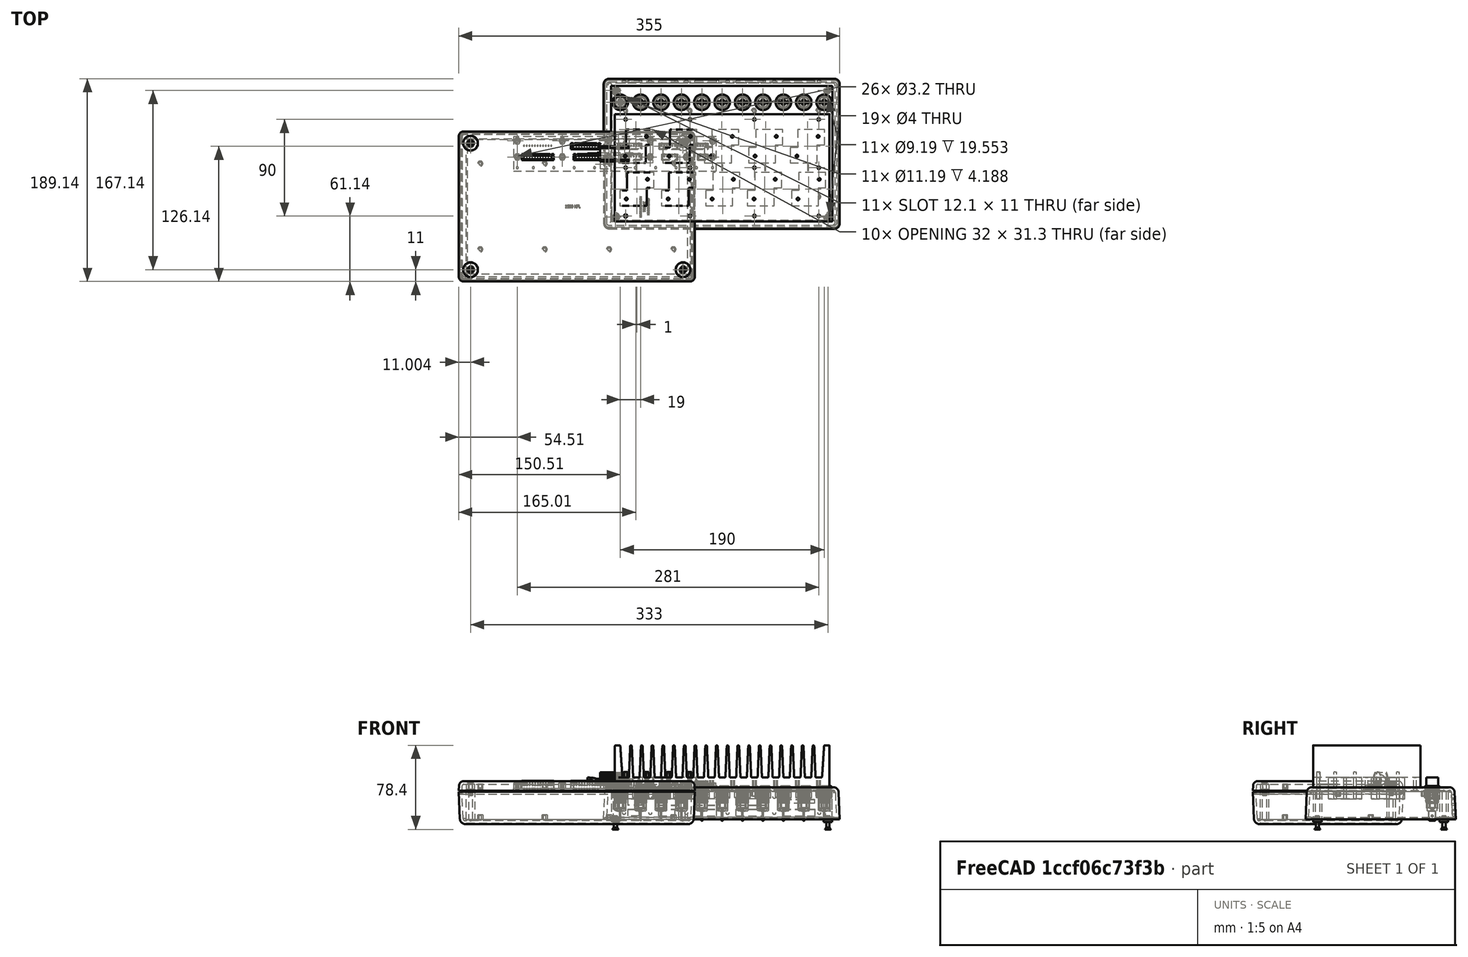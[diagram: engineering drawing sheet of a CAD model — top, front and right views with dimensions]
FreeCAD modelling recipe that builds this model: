
FCSTD DOCUMENT  (FreeCAD 0.20R29410 (Git))
Label: LiPoKiller
License: All rights reserved
LicenseURL: http://en.wikipedia.org/wiki/All_rights_reserved
objects: TechDraw::DrawViewDimension×84, Part::Feature×76, App::Part×52, Part::FeaturePython×17, Sketcher::SketchObject×12, Part::Extrusion×12, Part::MultiFuse×5, TechDraw::DrawSVGTemplate×4, TechDraw::DrawProjGroupItem×4, TechDraw::DrawProjGroup×4, TechDraw::DrawPage×4, Part::Cut×3, App::DocumentObjectGroup×2, Spreadsheet::Sheet×1, PartDesign::CoordinateSystem×1, App::FeaturePython×1, TechDraw::DrawViewBalloon×1
note: 111 computed .brp shape members not serialized (recipe doc carries the construction recipe); baked Part::Feature solids carry a one-line shape summary decoded from their .brp

FEATURE [Spreadsheet::Sheet] Spreadsheet  label="Param"
  cells = A1=R_Grid_Along; B1(R_Grid_Along)=40; A2=R_Grid_Across; B2(R_Grid_Across)=40; A3=R_nof_Along; B3(R_nof_Along)=2; A4=R_nof_Across; B4(R_nof_Across)=5; A5=R_Offset; B5(R_Offset)=1; A6=R_Body_Length; B6(R_Body_Length)=27.3; A7=R_Body_Width; B7(R_Body_Width)=14.2; A8=R_Tab_Length; B8(R_Tab_Length)=10.4; A9=R_Tab_Width; B9(R_Tab_Width)==(28 - 14.2) / 2; A10=R_Clearance; B10(R_Clearance)=2; A11=R_Hole_Along; B11(R_Hole_Along)=18.3; A12=R_Hole_Across; B12(R_Hole_Across)=19.8; A13=R_Hole_Size; B13(R_Hole_Size)=2.5; A14=R_Thread; B14(R_Thread)=M3; A15=Heatsink_Length; B15(Heatsink_Length)=200; A16=Heatsing_Width; B16(Heatsink_Width)=100; A17=Heatsink_Shift; B17(Heatsink_Shift)==26 / 2; A18=Con_Grid; B18(Con_Grid)=19; A19=Con_Pos_y; B19(Con_Pos_y)=48; A20=Con_nof; B20(Con_nof)=11; A21=Con_Diameter; B21(Con_Diameter)=12.1; A22=Con_Width; B22(Con_Width)=11; A23=Heatsink_Hole; B23(Heatsink_Hole)=3.2; A24=Heatsink_Thread_Hole; B24(Heatsink_Thread_Hole)=2.5; A25=Heatsink_Thread; B25(Heatsink_Thread)=M3; A26=Heatsink_Hole_nof_x; B26(Heatsink_Hole_nof_x)=4; A27=Heatsink_Hole_nof_y; B27(Heatsink_Hole_nof_y)=3; A28=Heatsink_Hole_Grid_x; B28(Heatsink_Hole_Grid_x)=60; A29=Heatsink_Hole_Grid_y; B29(Heatsink_Hole_Grid_y)=45; A30=Heatsink_Hole_Offset; B30(Heatsink_Hole_Offset)=5; A31=Balancer_Width; B31(Balancer_Width)=5.75; A32=Balancer_Length_Offset; B32(Balancer_Length_Offset)=2.4; A33=Balancer_Length_Increment; B33(Balancer_Length_Increment)=2.5; A34=Balancer_Clearance; B34(Balancer_Clearance)=0.2; A35=Balancer_Grid; B35(Balancer_Grid)=10; A36=Balancer_Distance; B36(Balancer_Distance)=16.1; A37=Balancer_Pin_Offset; B37(Balancer_Pin_Offset)=3.4; A38=Balancer_Mil_Size; B38(Balancer_Mil_Size)=2.54; A39=Balancer_Mil_Clearance; B39(Balancer_Mil_Clearance)=0.5; A40=Balancer_X; B40(Balancer_X)=72; A41=Balancer_Y; B41(Balancer_Y)=7.5; A42=Panel_Mount_Diameter; B42(Panel_Mount_Diameter)=3.2; A43=Panel_Mount_X; B43(Panel_Mount_X)=91; A44=Panel_Mount_Y; B44(Panel_Mount_Y)=12; A45=Panel_Length; B45(Panel_Length)=189; A46=Panel_Width; B46(Panel_Width)=32
FEATURE [Sketcher::SketchObject] Sketch
  FullyConstrained = true
  expr: Constraints[10] = <<Param>>.R_Tab_Width
  expr: Constraints[11] = <<Param>>.R_Tab_Width
  expr: Constraints[12] = <<Param>>.R_Tab_Length + 2 * <<Param>>.R_Clearance
  expr: Constraints[13] = <<Param>>.R_Tab_Length + 2 * <<Param>>.R_Clearance
  expr: Constraints[20] = <<Param>>.R_Grid_Along * (<<Param>>.R_nof_Along - 1) / 2 + <<Param>>.Heatsink_Shift
  expr: Constraints[29] = <<Param>>.Heatsink_Length / 2 - <<Param>>.R_Grid_Across * (<<Param>>.R_nof_Across - 1) / 2 + <<Param>>.R_Offset / 2
  expr: Constraints[8] = Spreadsheet.R_Body_Width + 2 * <<Param>>.R_Clearance
  expr: Constraints[9] = <<Param>>.R_Body_Length + 2 * <<Param>>.R_Clearance
  sketch-geometry (11):
    g0: LineSegment StartX=4.5 StartY=-48.65 StartZ=0 EndX=29.6 EndY=-48.65 EndZ=0
    g1: LineSegment StartX=29.6 StartY=-48.65 StartZ=0 EndX=29.6 EndY=-31.75 EndZ=0
    g2: LineSegment StartX=29.6 StartY=-31.75 StartZ=0 EndX=36.5 EndY=-31.75 EndZ=0
    g3: LineSegment StartX=36.5 StartY=-31.75 StartZ=0 EndX=36.5 EndY=-17.35 EndZ=0
    g4: LineSegment StartX=36.5 StartY=-17.35 StartZ=0 EndX=11.4 EndY=-17.35 EndZ=0
    g5: LineSegment StartX=11.4 StartY=-17.35 StartZ=0 EndX=11.4 EndY=-34.25 EndZ=0
    g6: LineSegment StartX=11.4 StartY=-34.25 StartZ=0 EndX=4.5 EndY=-34.25 EndZ=0
    g7: LineSegment StartX=4.5 StartY=-34.25 StartZ=0 EndX=4.5 EndY=-48.65 EndZ=0
    g8: LineSegment StartX=11.4 StartY=-17.35 StartZ=0 EndX=29.6 EndY=-48.65 EndZ=0
    g9: LineSegment StartX=11.4 StartY=-34.25 StartZ=0 EndX=29.6 EndY=-31.75 EndZ=0
    g10: GeomPoint X=20.5 Y=-33 Z=0
  constraints (30):
    c: Coincident(g0,g1)
    c: Coincident(g1,g2)
    c: Coincident(g2,g3)
    c: Coincident(g3,g4)
    c: Coincident(g4,g5)
    c: Coincident(g5,g6)
    c: Coincident(g6,g7)
    c: Coincident(g7,g0)
    c: Distance(g5,g1) = 18.2
    c: Distance(g4,g0) = 31.3
    c: Distance(g6,g5) = 6.9
    c: Distance(g1,g2) = 6.9
    c: Distance(g3,g2) = 14.4
    c: Distance(g6,g0) = 14.4
    c: Coincident(g8,g4)
    c: Coincident(g9,g5)
    c: Coincident(g9,g1)
    c: Coincident(g8,g0)
    c: PointOnObject(g10,g9)
    c: PointOnObject(g10,g8)
    c: Distance(g10,g-1) = 33
    c: Perpendicular(g0,g7)
    c: Perpendicular(g0,g1)
    c: Perpendicular(g2,g1)
    c: Perpendicular(g2,g3)
    c: Perpendicular(g3,g4)
    c: Perpendicular(g4,g5)
    c: Perpendicular(g5,g6)
    c: Horizontal(g4)
    c: Distance(g10,g-2) = 20.5
FEATURE [Part::Extrusion] Extrude
  Base = -> Sketch
  Dir = (0,0,1)
  DirMode = 2
  FaceMakerClass = Part::FaceMakerBullseye
  LengthFwd = 10
  LengthRev = 10
  Solid = true
  Symmetric = false
FEATURE [Part::FeaturePython] Array001  # Draft array (typed FeaturePython)
  AlwaysSyncPlacement = false
  Angle = 360
  ArrayType = 0
  Axis = (0,0,1)
  Base = -> Extrude
  Center = (0,0,0)
  Count = 3
  ExpandArray = false
  Fuse = false
  IntervalAxis = (0,0,0)
  IntervalX = (80,0,0)
  IntervalY = (0,80,0)
  IntervalZ = (0,0,0)
  NumberCircles = 3
  NumberPolar = 5
  NumberX = 3
  NumberY = 1
  NumberZ = 1
  PlacementList = 3 placements: arithmetic series from (0,0,0) step (80,0,0) to (160,0,0)
  RadialDistance = 50
  ScaleList = (3) [(1,1,1),(1,1,1),(1,1,1)]
  Symmetry = 1
  TangentialDistance = 25
  expr: .IntervalX.x = <<Param>>.R_Grid_Across * 2
  expr: .IntervalY.y = <<Param>>.R_Grid_Along * 2
  expr: NumberX = ceil(<<Param>>.R_nof_Across / 2)
  expr: NumberY = ceil(<<Param>>.R_nof_Along / 2)
FEATURE [Sketcher::SketchObject] Sketch001
  FullyConstrained = true
  expr: Constraints[10] = <<Param>>.R_Tab_Width
  expr: Constraints[11] = <<Param>>.R_Tab_Width
  expr: Constraints[12] = <<Param>>.R_Tab_Length + 2 * <<Param>>.R_Clearance
  expr: Constraints[13] = <<Param>>.R_Tab_Length + 2 * <<Param>>.R_Clearance
  expr: Constraints[20] = <<Param>>.R_Grid_Along * (<<Param>>.R_nof_Along - 1) / 2 + <<Param>>.Heatsink_Shift
  expr: Constraints[29] = <<Param>>.Heatsink_Length / 2 - <<Param>>.R_Grid_Across * (<<Param>>.R_nof_Across - 3) / 2 - <<Param>>.R_Offset / 2
  expr: Constraints[8] = Spreadsheet.R_Body_Width + 2 * <<Param>>.R_Clearance
  expr: Constraints[9] = <<Param>>.R_Body_Length + 2 * <<Param>>.R_Clearance
  sketch-geometry (11):
    g0: LineSegment StartX=43.5 StartY=-48.65 StartZ=0 EndX=68.6 EndY=-48.65 EndZ=0
    g1: LineSegment StartX=68.6 StartY=-48.65 StartZ=0 EndX=68.6 EndY=-31.75 EndZ=0
    g2: LineSegment StartX=68.6 StartY=-31.75 StartZ=0 EndX=75.5 EndY=-31.75 EndZ=0
    g3: LineSegment StartX=75.5 StartY=-31.75 StartZ=0 EndX=75.5 EndY=-17.35 EndZ=0
    g4: LineSegment StartX=75.5 StartY=-17.35 StartZ=0 EndX=50.4 EndY=-17.35 EndZ=0
    g5: LineSegment StartX=50.4 StartY=-17.35 StartZ=0 EndX=50.4 EndY=-34.25 EndZ=0
    g6: LineSegment StartX=50.4 StartY=-34.25 StartZ=0 EndX=43.5 EndY=-34.25 EndZ=0
    g7: LineSegment StartX=43.5 StartY=-34.25 StartZ=0 EndX=43.5 EndY=-48.65 EndZ=0
    g8: LineSegment StartX=50.4 StartY=-17.35 StartZ=0 EndX=68.6 EndY=-48.65 EndZ=0
    g9: LineSegment StartX=50.4 StartY=-34.25 StartZ=0 EndX=68.6 EndY=-31.75 EndZ=0
    g10: GeomPoint X=59.5 Y=-33 Z=0
  constraints (30):
    c: Coincident(g0,g1)
    c: Coincident(g1,g2)
    c: Coincident(g2,g3)
    c: Coincident(g3,g4)
    c: Coincident(g4,g5)
    c: Coincident(g5,g6)
    c: Coincident(g6,g7)
    c: Coincident(g7,g0)
    c: Distance(g5,g1) = 18.2
    c: Distance(g4,g0) = 31.3
    c: Distance(g6,g5) = 6.9
    c: Distance(g1,g2) = 6.9
    c: Distance(g3,g2) = 14.4
    c: Distance(g6,g0) = 14.4
    c: Coincident(g8,g4)
    c: Coincident(g9,g5)
    c: Coincident(g9,g1)
    c: Coincident(g8,g0)
    c: PointOnObject(g10,g9)
    c: PointOnObject(g10,g8)
    c: Distance(g10,g-1) = 33
    c: Perpendicular(g0,g7)
    c: Perpendicular(g0,g1)
    c: Perpendicular(g2,g1)
    c: Perpendicular(g2,g3)
    c: Perpendicular(g3,g4)
    c: Perpendicular(g4,g5)
    c: Perpendicular(g5,g6)
    c: Horizontal(g4)
    c: Distance(g10,g-2) = 59.5
FEATURE [Part::Extrusion] Extrude001
  Base = -> Sketch001
  Dir = (0,0,1)
  DirMode = 2
  FaceMakerClass = Part::FaceMakerBullseye
  LengthFwd = 10
  LengthRev = 10
  Solid = true
  Symmetric = false
FEATURE [Part::FeaturePython] Array002  # Draft array (typed FeaturePython)
  AlwaysSyncPlacement = false
  Angle = 360
  ArrayType = 0
  Axis = (0,0,1)
  Base = -> Extrude001
  Center = (0,0,0)
  Count = 2
  ExpandArray = false
  Fuse = false
  IntervalAxis = (0,0,0)
  IntervalX = (80,0,0)
  IntervalY = (0,80,0)
  IntervalZ = (0,0,0)
  NumberCircles = 3
  NumberPolar = 5
  NumberX = 2
  NumberY = 1
  NumberZ = 1
  PlacementList = 2 placements: [(0,0,0),(80,0,0)]
  RadialDistance = 50
  ScaleList = (2) [(1,1,1),(1,1,1)]
  Symmetry = 1
  TangentialDistance = 25
  expr: .IntervalX.x = <<Param>>.R_Grid_Across * 2
  expr: .IntervalY.y = <<Param>>.R_Grid_Along * 2
  expr: NumberX = floor(<<Param>>.R_nof_Across / 2)
  expr: NumberY = floor(<<Param>>.R_nof_Along / 2)
FEATURE [Sketcher::SketchObject] Sketch002
  FullyConstrained = true
  expr: Constraints[10] = <<Param>>.R_Tab_Width
  expr: Constraints[11] = <<Param>>.R_Tab_Width
  expr: Constraints[12] = <<Param>>.R_Tab_Length + 2 * <<Param>>.R_Clearance
  expr: Constraints[13] = <<Param>>.R_Tab_Length + 2 * <<Param>>.R_Clearance
  expr: Constraints[28] = <<Param>>.Heatsink_Length / 2 - <<Param>>.R_Grid_Across * (<<Param>>.R_nof_Across - 1) / 2 - <<Param>>.R_Offset / 2
  expr: Constraints[31] = <<Param>>.R_Grid_Along * (<<Param>>.R_nof_Along - 1) / 2 + <<Param>>.Heatsink_Shift
  expr: Constraints[33] = <<Param>>.R_Grid_Along
  expr: Constraints[8] = Spreadsheet.R_Body_Width + 2 * <<Param>>.R_Clearance
  expr: Constraints[9] = <<Param>>.R_Body_Length + 2 * <<Param>>.R_Clearance
  sketch-geometry (12):
    g0: LineSegment StartX=3.5 StartY=-8.65 StartZ=0 EndX=28.6 EndY=-8.65 EndZ=0
    g1: LineSegment StartX=28.6 StartY=-8.65 StartZ=0 EndX=28.6 EndY=8.25 EndZ=0
    g2: LineSegment StartX=28.6 StartY=8.25 StartZ=0 EndX=35.5 EndY=8.25 EndZ=0
    g3: LineSegment StartX=35.5 StartY=8.25 StartZ=0 EndX=35.5 EndY=22.65 EndZ=0
    g4: LineSegment StartX=35.5 StartY=22.65 StartZ=0 EndX=10.4 EndY=22.65 EndZ=0
    g5: LineSegment StartX=10.4 StartY=22.65 StartZ=0 EndX=10.4 EndY=5.75 EndZ=0
    g6: LineSegment StartX=10.4 StartY=5.75 StartZ=0 EndX=3.5 EndY=5.75 EndZ=0
    g7: LineSegment StartX=3.5 StartY=5.75 StartZ=0 EndX=3.5 EndY=-8.65 EndZ=0
    g8: LineSegment StartX=10.4 StartY=22.65 StartZ=0 EndX=28.6 EndY=-8.65 EndZ=0
    g9: LineSegment StartX=10.4 StartY=5.75 StartZ=0 EndX=28.6 EndY=8.25 EndZ=0
    g10: GeomPoint X=19.5 Y=7 Z=0
    g11: LineSegment StartX=0 StartY=-33 StartZ=0 EndX=200 EndY=-33 EndZ=0
  constraints (34):
    c: Coincident(g0,g1)
    c: Coincident(g1,g2)
    c: Coincident(g2,g3)
    c: Coincident(g3,g4)
    c: Coincident(g4,g5)
    c: Coincident(g5,g6)
    c: Coincident(g6,g7)
    c: Coincident(g7,g0)
    c: Distance(g5,g1) = 18.2
    c: Distance(g4,g0) = 31.3
    c: Distance(g6,g5) = 6.9
    c: Distance(g1,g2) = 6.9
    c: Distance(g3,g2) = 14.4
    c: Distance(g6,g0) = 14.4
    c: Coincident(g8,g4)
    c: Coincident(g9,g5)
    c: Coincident(g9,g1)
    c: Coincident(g8,g0)
    c: PointOnObject(g10,g9)
    c: PointOnObject(g10,g8)
    c: Perpendicular(g0,g7)
    c: Perpendicular(g0,g1)
    c: Perpendicular(g2,g1)
    c: Perpendicular(g2,g3)
    c: Perpendicular(g3,g4)
    c: Perpendicular(g4,g5)
    c: Perpendicular(g5,g6)
    c: Horizontal(g4)
    c: Distance(g10,g-2) = 19.5
    c: PointOnObject(g11,g-2)
    c: Horizontal(g11)
    c: Distance(g11,g-1) = 33
    c: Distance(g11,g-2) = 200
    c: Distance(g10,g11) = 40
FEATURE [Part::Extrusion] Extrude002
  Base = -> Sketch002
  Dir = (0,0,1)
  DirMode = 2
  FaceMakerClass = Part::FaceMakerBullseye
  LengthFwd = 10
  LengthRev = 10
  Solid = true
  Symmetric = false
FEATURE [Part::FeaturePython] Array003  # Draft array (typed FeaturePython)
  AlwaysSyncPlacement = false
  Angle = 360
  ArrayType = 0
  Axis = (0,0,1)
  Base = -> Extrude002
  Center = (0,0,0)
  Count = 3
  ExpandArray = false
  Fuse = false
  IntervalAxis = (0,0,0)
  IntervalX = (80,0,0)
  IntervalY = (0,80,0)
  IntervalZ = (0,0,0)
  NumberCircles = 3
  NumberPolar = 5
  NumberX = 3
  NumberY = 1
  NumberZ = 1
  PlacementList = 3 placements: arithmetic series from (0,0,0) step (80,0,0) to (160,0,0)
  RadialDistance = 50
  ScaleList = (3) [(1,1,1),(1,1,1),(1,1,1)]
  Symmetry = 1
  TangentialDistance = 25
  expr: .IntervalX.x = <<Param>>.R_Grid_Across * 2
  expr: .IntervalY.y = <<Param>>.R_Grid_Along * 2
  expr: NumberX = ceil(<<Param>>.R_nof_Across / 2)
  expr: NumberY = floor(<<Param>>.R_nof_Along / 2)
FEATURE [Sketcher::SketchObject] Sketch003
  FullyConstrained = true
  expr: Constraints[10] = <<Param>>.R_Tab_Width
  expr: Constraints[11] = <<Param>>.R_Tab_Width
  expr: Constraints[12] = <<Param>>.R_Tab_Length + 2 * <<Param>>.R_Clearance
  expr: Constraints[13] = <<Param>>.R_Tab_Length + 2 * <<Param>>.R_Clearance
  expr: Constraints[28] = <<Param>>.Heatsink_Length / 2 - <<Param>>.R_Grid_Across * (<<Param>>.R_nof_Across - 3) / 2 + <<Param>>.R_Offset / 2
  expr: Constraints[31] = <<Param>>.R_Grid_Along * (<<Param>>.R_nof_Along - 1) / 2 + <<Param>>.Heatsink_Shift
  expr: Constraints[33] = <<Param>>.R_Grid_Along
  expr: Constraints[8] = Spreadsheet.R_Body_Width + 2 * <<Param>>.R_Clearance
  expr: Constraints[9] = <<Param>>.R_Body_Length + 2 * <<Param>>.R_Clearance
  sketch-geometry (12):
    g0: LineSegment StartX=44.5 StartY=-8.65 StartZ=0 EndX=69.6 EndY=-8.65 EndZ=0
    g1: LineSegment StartX=69.6 StartY=-8.65 StartZ=0 EndX=69.6 EndY=8.25 EndZ=0
    g2: LineSegment StartX=69.6 StartY=8.25 StartZ=0 EndX=76.5 EndY=8.25 EndZ=0
    g3: LineSegment StartX=76.5 StartY=8.25 StartZ=0 EndX=76.5 EndY=22.65 EndZ=0
    g4: LineSegment StartX=76.5 StartY=22.65 StartZ=0 EndX=51.4 EndY=22.65 EndZ=0
    g5: LineSegment StartX=51.4 StartY=22.65 StartZ=0 EndX=51.4 EndY=5.75 EndZ=0
    g6: LineSegment StartX=51.4 StartY=5.75 StartZ=0 EndX=44.5 EndY=5.75 EndZ=0
    g7: LineSegment StartX=44.5 StartY=5.75 StartZ=0 EndX=44.5 EndY=-8.65 EndZ=0
    g8: LineSegment StartX=51.4 StartY=22.65 StartZ=0 EndX=69.6 EndY=-8.65 EndZ=0
    g9: LineSegment StartX=51.4 StartY=5.75 StartZ=0 EndX=69.6 EndY=8.25 EndZ=0
    g10: GeomPoint X=60.5 Y=7 Z=0
    g11: LineSegment StartX=0 StartY=-33 StartZ=0 EndX=200 EndY=-33 EndZ=0
  constraints (34):
    c: Coincident(g0,g1)
    c: Coincident(g1,g2)
    c: Coincident(g2,g3)
    c: Coincident(g3,g4)
    c: Coincident(g4,g5)
    c: Coincident(g5,g6)
    c: Coincident(g6,g7)
    c: Coincident(g7,g0)
    c: Distance(g5,g1) = 18.2
    c: Distance(g4,g0) = 31.3
    c: Distance(g6,g5) = 6.9
    c: Distance(g1,g2) = 6.9
    c: Distance(g3,g2) = 14.4
    c: Distance(g6,g0) = 14.4
    c: Coincident(g8,g4)
    c: Coincident(g9,g5)
    c: Coincident(g9,g1)
    c: Coincident(g8,g0)
    c: PointOnObject(g10,g9)
    c: PointOnObject(g10,g8)
    c: Perpendicular(g0,g7)
    c: Perpendicular(g0,g1)
    c: Perpendicular(g2,g1)
    c: Perpendicular(g2,g3)
    c: Perpendicular(g3,g4)
    c: Perpendicular(g4,g5)
    c: Perpendicular(g5,g6)
    c: Horizontal(g4)
    c: Distance(g10,g-2) = 60.5
    c: PointOnObject(g11,g-2)
    c: Horizontal(g11)
    c: Distance(g11,g-1) = 33
    c: Distance(g11,g-2) = 200
    c: Distance(g10,g11) = 40
FEATURE [Part::Extrusion] Extrude003
  Base = -> Sketch003
  Dir = (0,0,1)
  DirMode = 2
  FaceMakerClass = Part::FaceMakerBullseye
  LengthFwd = 10
  LengthRev = 10
  Solid = true
  Symmetric = false
FEATURE [Part::FeaturePython] Array004  # Draft array (typed FeaturePython)
  AlwaysSyncPlacement = false
  Angle = 360
  ArrayType = 0
  Axis = (0,0,1)
  Base = -> Extrude003
  Center = (0,0,0)
  Count = 2
  ExpandArray = false
  Fuse = false
  IntervalAxis = (0,0,0)
  IntervalX = (80,0,0)
  IntervalY = (0,80,0)
  IntervalZ = (0,0,0)
  NumberCircles = 3
  NumberPolar = 5
  NumberX = 2
  NumberY = 1
  NumberZ = 1
  PlacementList = 2 placements: [(0,0,0),(80,0,0)]
  RadialDistance = 50
  ScaleList = (2) [(1,1,1),(1,1,1)]
  Symmetry = 1
  TangentialDistance = 25
  expr: .IntervalX.x = <<Param>>.R_Grid_Across * 2
  expr: .IntervalY.y = <<Param>>.R_Grid_Along * 2
  expr: NumberX = floor(<<Param>>.R_nof_Across / 2)
  expr: NumberY = floor(<<Param>>.R_nof_Along / 2)
FEATURE [Part::Feature] Part__Feature012  label="Resistor Arcol HS"
  shape: bbox 27.3 x 28 x 14.8 mm, 83 faces (baked)
FEATURE [Part::Feature] Part__Feature013  label="Resistor Arcol HS001"
  shape: bbox 33.3 x 2.1 x 2.1 mm, 3 faces (baked)
FEATURE [Part::Feature] Part__Feature014  label="Resistor Arcol HS002"
  shape: bbox 8.85 x 0.8 x 4.5 mm, 7 faces (baked)
FEATURE [Part::Feature] Part__Feature015  label="Resistor Arcol HS003"
  shape: bbox 8.85 x 0.8 x 4.5 mm, 7 faces (baked)
FEATURE [Part::Feature] Part__Feature016  label="Resistor Arcol HS004"
  shape: bbox 27.3 x 9.23 x 9.23 mm, 6 faces, 0 solids (baked)
FEATURE [App::Part] Resistor_Arcol_HS  label="Resistor Arcol HS005"
  Group = -> [Part__Feature012,Part__Feature013,Part__Feature014,Part__Feature015,Part__Feature016]
  Origin = -> Origin002
  Placement = pos=(20.5,-33,2.8e-15) rot=(0.707107,0.707107,0;3.14159rad)
  expr: .Placement.Base.x = <<Param>>.Heatsink_Length / 2 - <<Param>>.R_Grid_Across * (<<Param>>.R_nof_Across - 1) / 2 + <<Param>>.R_Offset / 2
  expr: .Placement.Base.y = -(<<Param>>.R_Grid_Along * (<<Param>>.R_nof_Along - 1) / 2 + <<Param>>.Heatsink_Shift)
FEATURE [Part::FeaturePython] Array005  # Draft array (typed FeaturePython)
  AlwaysSyncPlacement = false
  Angle = 360
  ArrayType = 0
  Axis = (0,0,1)
  Base = -> Resistor_Arcol_HS
  Center = (0,0,0)
  Count = 3
  ExpandArray = false
  Fuse = false
  IntervalAxis = (0,0,0)
  IntervalX = (80,0,0)
  IntervalY = (0,80,0)
  IntervalZ = (0,0,0)
  NumberCircles = 3
  NumberPolar = 5
  NumberX = 3
  NumberY = 1
  NumberZ = 1
  PlacementList = 3 placements: arithmetic series from (20.5,-33,2.8e-15) step (80,0,0) to (180.5,-33,2.8e-15)
  RadialDistance = 50
  ScaleList = (3) [(1,1,1),(1,1,1),(1,1,1)]
  Symmetry = 1
  TangentialDistance = 25
  expr: .IntervalX.x = <<Param>>.R_Grid_Across * 2
  expr: .IntervalY.y = <<Param>>.R_Grid_Along * 2
  expr: NumberX = ceil(<<Param>>.R_nof_Across / 2)
  expr: NumberY = ceil(<<Param>>.R_nof_Along / 2)
FEATURE [Part::Feature] Part__Feature017  label="Resistor Arcol HS006"
  shape: bbox 27.3 x 28 x 14.8 mm, 83 faces (baked)
FEATURE [Part::Feature] Part__Feature018  label="Resistor Arcol HS007"
  shape: bbox 33.3 x 2.1 x 2.1 mm, 3 faces (baked)
FEATURE [Part::Feature] Part__Feature019  label="Resistor Arcol HS008"
  shape: bbox 8.85 x 0.8 x 4.5 mm, 7 faces (baked)
FEATURE [Part::Feature] Part__Feature020  label="Resistor Arcol HS009"
  shape: bbox 8.85 x 0.8 x 4.5 mm, 7 faces (baked)
FEATURE [Part::Feature] Part__Feature021  label="Resistor Arcol HS010"
  shape: bbox 27.3 x 9.23 x 9.23 mm, 6 faces, 0 solids (baked)
FEATURE [App::Part] Resistor_Arcol_HS001  label="Resistor Arcol HS011"
  Group = -> [Part__Feature017,Part__Feature018,Part__Feature019,Part__Feature020,Part__Feature021]
  Origin = -> Origin003
  Placement = pos=(59.5,-33,2.8e-15) rot=(0.707107,0.707107,0;3.14159rad)
  expr: .Placement.Base.x = <<Param>>.Heatsink_Length / 2 - <<Param>>.R_Grid_Across * (<<Param>>.R_nof_Across - 3) / 2 - <<Param>>.R_Offset / 2
  expr: .Placement.Base.y = -(<<Param>>.R_Grid_Along * (<<Param>>.R_nof_Along - 1) / 2 + <<Param>>.Heatsink_Shift)
FEATURE [Part::FeaturePython] Array006  # Draft array (typed FeaturePython)
  AlwaysSyncPlacement = false
  Angle = 360
  ArrayType = 0
  Axis = (0,0,1)
  Base = -> Resistor_Arcol_HS001
  Center = (0,0,0)
  Count = 2
  ExpandArray = false
  Fuse = false
  IntervalAxis = (0,0,0)
  IntervalX = (80,0,0)
  IntervalY = (0,80,0)
  IntervalZ = (0,0,0)
  NumberCircles = 3
  NumberPolar = 5
  NumberX = 2
  NumberY = 1
  NumberZ = 1
  PlacementList = 2 placements: [(59.5,-33,2.8e-15),(139.5,-33,2.8e-15)]
  RadialDistance = 50
  ScaleList = (2) [(1,1,1),(1,1,1)]
  Symmetry = 1
  TangentialDistance = 25
  expr: .IntervalX.x = <<Param>>.R_Grid_Across * 2
  expr: .IntervalY.y = <<Param>>.R_Grid_Along * 2
  expr: NumberX = floor(<<Param>>.R_nof_Across / 2)
  expr: NumberY = floor(<<Param>>.R_nof_Along / 2)
FEATURE [Part::Feature] Part__Feature022  label="Resistor Arcol HS012"
  shape: bbox 27.3 x 28 x 14.8 mm, 83 faces (baked)
FEATURE [Part::Feature] Part__Feature023  label="Resistor Arcol HS013"
  shape: bbox 33.3 x 2.1 x 2.1 mm, 3 faces (baked)
FEATURE [Part::Feature] Part__Feature024  label="Resistor Arcol HS014"
  shape: bbox 8.85 x 0.8 x 4.5 mm, 7 faces (baked)
FEATURE [Part::Feature] Part__Feature025  label="Resistor Arcol HS015"
  shape: bbox 8.85 x 0.8 x 4.5 mm, 7 faces (baked)
FEATURE [Part::Feature] Part__Feature026  label="Resistor Arcol HS016"
  shape: bbox 27.3 x 9.23 x 9.23 mm, 6 faces, 0 solids (baked)
FEATURE [App::Part] Resistor_Arcol_HS002  label="Resistor Arcol HS017"
  Group = -> [Part__Feature022,Part__Feature023,Part__Feature024,Part__Feature025,Part__Feature026]
  Origin = -> Origin004
  Placement = pos=(19.5,7,2.8e-15) rot=(0.707107,0.707107,0;3.14159rad)
  expr: .Placement.Base.x = <<Param>>.Heatsink_Length / 2 - <<Param>>.R_Grid_Across * (<<Param>>.R_nof_Across - 1) / 2 - <<Param>>.R_Offset / 2
  expr: .Placement.Base.y = -(<<Param>>.R_Grid_Along * (<<Param>>.R_nof_Along - 1) / 2 + <<Param>>.Heatsink_Shift) + <<Param>>.R_Grid_Along
FEATURE [Part::FeaturePython] Array007  # Draft array (typed FeaturePython)
  AlwaysSyncPlacement = false
  Angle = 360
  ArrayType = 0
  Axis = (0,0,1)
  Base = -> Resistor_Arcol_HS002
  Center = (0,0,0)
  Count = 3
  ExpandArray = false
  Fuse = false
  IntervalAxis = (0,0,0)
  IntervalX = (80,0,0)
  IntervalY = (0,80,0)
  IntervalZ = (0,0,0)
  NumberCircles = 3
  NumberPolar = 5
  NumberX = 3
  NumberY = 1
  NumberZ = 1
  PlacementList = 3 placements: arithmetic series from (19.5,7,2.8e-15) step (80,0,0) to (179.5,7,2.8e-15)
  RadialDistance = 50
  ScaleList = (3) [(1,1,1),(1,1,1),(1,1,1)]
  Symmetry = 1
  TangentialDistance = 25
  expr: .IntervalX.x = <<Param>>.R_Grid_Across * 2
  expr: .IntervalY.y = <<Param>>.R_Grid_Along * 2
  expr: NumberX = ceil(<<Param>>.R_nof_Across / 2)
  expr: NumberY = floor(<<Param>>.R_nof_Along / 2)
FEATURE [Part::Feature] Part__Feature027  label="Resistor Arcol HS018"
  shape: bbox 27.3 x 28 x 14.8 mm, 83 faces (baked)
FEATURE [Part::Feature] Part__Feature028  label="Resistor Arcol HS019"
  shape: bbox 33.3 x 2.1 x 2.1 mm, 3 faces (baked)
FEATURE [Part::Feature] Part__Feature029  label="Resistor Arcol HS020"
  shape: bbox 8.85 x 0.8 x 4.5 mm, 7 faces (baked)
FEATURE [Part::Feature] Part__Feature030  label="Resistor Arcol HS021"
  shape: bbox 8.85 x 0.8 x 4.5 mm, 7 faces (baked)
FEATURE [Part::Feature] Part__Feature031  label="Resistor Arcol HS022"
  shape: bbox 27.3 x 9.23 x 9.23 mm, 6 faces, 0 solids (baked)
FEATURE [App::Part] Resistor_Arcol_HS003  label="Resistor Arcol HS023"
  Group = -> [Part__Feature027,Part__Feature028,Part__Feature029,Part__Feature030,Part__Feature031]
  Origin = -> Origin005
  Placement = pos=(60.5,7,2.8e-15) rot=(0.707107,0.707107,0;3.14159rad)
  expr: .Placement.Base.x = <<Param>>.Heatsink_Length / 2 - <<Param>>.R_Grid_Across * (<<Param>>.R_nof_Across - 3) / 2 + <<Param>>.R_Offset / 2
  expr: .Placement.Base.y = -(<<Param>>.R_Grid_Along * (<<Param>>.R_nof_Along - 1) / 2 + <<Param>>.Heatsink_Shift) + <<Param>>.R_Grid_Along
FEATURE [Part::FeaturePython] Array008  # Draft array (typed FeaturePython)
  AlwaysSyncPlacement = false
  Angle = 360
  ArrayType = 0
  Axis = (0,0,1)
  Base = -> Resistor_Arcol_HS003
  Center = (0,0,0)
  Count = 2
  ExpandArray = false
  Fuse = false
  IntervalAxis = (0,0,0)
  IntervalX = (80,0,0)
  IntervalY = (0,80,0)
  IntervalZ = (0,0,0)
  NumberCircles = 3
  NumberPolar = 5
  NumberX = 2
  NumberY = 1
  NumberZ = 1
  PlacementList = 2 placements: [(60.5,7,2.8e-15),(140.5,7,2.8e-15)]
  RadialDistance = 50
  ScaleList = (2) [(1,1,1),(1,1,1)]
  Symmetry = 1
  TangentialDistance = 25
  expr: .IntervalX.x = <<Param>>.R_Grid_Across * 2
  expr: .IntervalY.y = <<Param>>.R_Grid_Along * 2
  expr: NumberX = floor(<<Param>>.R_nof_Across / 2)
  expr: NumberY = floor(<<Param>>.R_nof_Along / 2)
FEATURE [Part::MultiFuse] Fusion
  Shapes = -> [Array001,Array002,Array003,Array004]
FEATURE [Sketcher::SketchObject] Sketch004
  FullyConstrained = true
  expr: Constraints[10] = <<Param>>.Con_Pos_y
  expr: Constraints[12] = <<Param>>.Heatsink_Length / 2 - <<Param>>.Con_Grid * (<<Param>>.Con_nof - 1) / 2
  expr: Constraints[6] = <<Param>>.Con_Diameter
  expr: Constraints[7] = <<Param>>.Con_Diameter
  expr: Constraints[8] = <<Param>>.Con_Width
  expr: Constraints[9] = <<Param>>.Con_Width / 2
  sketch-geometry (4):
    g0: ArcOfCircle CenterX=5 CenterY=48 CenterZ=0 NormalX=0 NormalY=0 NormalZ=1 AngleXU=0 Radius=6.05 StartAngle=2.0005 EndAngle=4.28269
    g1: ArcOfCircle CenterX=5 CenterY=48 CenterZ=0 NormalX=0 NormalY=0 NormalZ=1 AngleXU=0 Radius=6.05 StartAngle=5.14209 EndAngle=7.42428
    g2: LineSegment StartX=2.47958 StartY=53.5 StartZ=0 EndX=7.52042 EndY=53.5 EndZ=0
    g3: LineSegment StartX=7.52042 StartY=42.5 StartZ=0 EndX=2.47958 EndY=42.5 EndZ=0
  constraints (13):
    c: Coincident(g1,g0)
    c: Coincident(g2,g0)
    c: Coincident(g2,g1)
    c: Coincident(g3,g1)
    c: Coincident(g3,g0)
    c: Horizontal(g3)
    c: Diameter(g1) = 12.1
    c: Diameter(g0) = 12.1
    c: Distance(g1,g3) = 11
    c: Distance(g0,g3) = 5.5
    c: Distance(g0,g-1) = 48
    c: Horizontal(g2)
    c: Distance(g0,g-2) = 5
FEATURE [Part::Extrusion] Extrude004
  Base = -> Sketch004
  Dir = (0,0,1)
  DirMode = 2
  FaceMakerClass = Part::FaceMakerBullseye
  LengthFwd = 10
  LengthRev = 10
  Solid = true
  Symmetric = false
FEATURE [Part::FeaturePython] Array009  # Draft array (typed FeaturePython)
  AlwaysSyncPlacement = false
  Angle = 360
  ArrayType = 0
  Axis = (0,0,1)
  Base = -> Extrude004
  Center = (0,0,0)
  Count = 11
  ExpandArray = false
  Fuse = false
  IntervalAxis = (0,0,0)
  IntervalX = (19,0,0)
  IntervalY = (0,100,0)
  IntervalZ = (0,0,100)
  NumberCircles = 3
  NumberPolar = 5
  NumberX = 11
  NumberY = 1
  NumberZ = 1
  PlacementList = 11 placements: arithmetic series from (0,0,0) step (19,0,0) to (190,0,0)
  RadialDistance = 50
  ScaleList = (11) [(1,1,1),(1,1,1),(1,1,1),(1,1,1),(1,1,1),(1,1,1),(1,1,1),(1,1,1),(1,1,1),(1,1,1),(1,1,1)]
  Symmetry = 1
  TangentialDistance = 25
FEATURE [Part::MultiFuse] Fusion001
  Shapes = -> [Array009,Fusion]
FEATURE [Sketcher::SketchObject] Sketch005
  FullyConstrained = true
  expr: Constraints[1] = <<Param>>.R_Grid_Along * (<<Param>>.R_nof_Along - 1) / 2 + <<Param>>.Heatsink_Shift
  expr: Constraints[26] = <<Param>>.R_Hole_Size
  expr: Constraints[27] = <<Param>>.R_Hole_Size
  expr: Constraints[28] = <<Param>>.R_Hole_Size
  expr: Constraints[29] = <<Param>>.R_Hole_Size
  expr: Constraints[2] = <<Param>>.Heatsink_Length / 2 - <<Param>>.R_Grid_Across * (<<Param>>.R_nof_Across - 1) / 2 + <<Param>>.R_Offset / 2
  expr: Constraints[30] = <<Param>>.R_Hole_Size
  expr: Constraints[31] = <<Param>>.R_Hole_Size
  expr: Constraints[32] = <<Param>>.R_Hole_Size
  expr: Constraints[33] = <<Param>>.R_Hole_Size
  expr: Constraints[8] = <<Param>>.R_Hole_Across
  expr: Constraints[9] = <<Param>>.R_Hole_Along
  sketch-geometry (12):
    g0: LineSegment StartX=30.4 StartY=-23.85 StartZ=0 EndX=10.6 EndY=-42.15 EndZ=0
    g1: GeomPoint X=20.5 Y=-33 Z=0
    g2: LineSegment StartX=20.5 StartY=-33 StartZ=0 EndX=30.4 EndY=-23.85 EndZ=0
    g3: LineSegment StartX=20.5 StartY=-33 StartZ=0 EndX=10.6 EndY=-42.15 EndZ=0
    g4: ArcOfCircle CenterX=30.4 CenterY=-23.85 CenterZ=0 NormalX=0 NormalY=0 NormalZ=1 AngleXU=0 Radius=1.25 StartAngle=1e-16 EndAngle=1.5708
    g5: ArcOfCircle CenterX=30.4 CenterY=-23.85 CenterZ=0 NormalX=0 NormalY=0 NormalZ=1 AngleXU=0 Radius=1.25 StartAngle=1.5708 EndAngle=3.14159
    g6: ArcOfCircle CenterX=30.4 CenterY=-23.85 CenterZ=0 NormalX=0 NormalY=0 NormalZ=1 AngleXU=0 Radius=1.25 StartAngle=3.14159 EndAngle=4.71239
    g7: ArcOfCircle CenterX=30.4 CenterY=-23.85 CenterZ=0 NormalX=0 NormalY=0 NormalZ=1 AngleXU=0 Radius=1.25 StartAngle=4.71239 EndAngle=6.28319
    g8: ArcOfCircle CenterX=10.6 CenterY=-42.15 CenterZ=0 NormalX=0 NormalY=0 NormalZ=1 AngleXU=0 Radius=1.25 StartAngle=0 EndAngle=1.5708
    g9: ArcOfCircle CenterX=10.6 CenterY=-42.15 CenterZ=0 NormalX=0 NormalY=0 NormalZ=1 AngleXU=0 Radius=1.25 StartAngle=1.5708 EndAngle=3.14159
    g10: ArcOfCircle CenterX=10.6 CenterY=-42.15 CenterZ=0 NormalX=0 NormalY=0 NormalZ=1 AngleXU=0 Radius=1.25 StartAngle=3.14159 EndAngle=4.71239
    g11: ArcOfCircle CenterX=10.6 CenterY=-42.15 CenterZ=0 NormalX=0 NormalY=0 NormalZ=1 AngleXU=0 Radius=1.25 StartAngle=4.71239 EndAngle=6.28319
  constraints (42):
    c: PointOnObject(g1,g0)
    c: Distance(g1,g-1) = 33
    c: Distance(g1,g-2) = 20.5
    c: Coincident(g2,g1)
    c: Coincident(g3,g1)
    c: Equal(g2,g3)
    c: Coincident(g0,g3)
    c: Coincident(g0,g2)
    c: DistanceX(g0,g0) = 19.8
    c: DistanceY(g0,g0) = 18.3
    c: Horizontal(g9,g9)
    c: Horizontal(g8,g8)
    c: Horizontal(g11,g11)
    c: Horizontal(g10,g10)
    c: Horizontal(g4,g4)
    c: Horizontal(g7,g7)
    c: Horizontal(g6,g6)
    c: Horizontal(g5,g5)
    c: Vertical(g5,g5)
    c: Vertical(g4,g4)
    c: Vertical(g7,g7)
    c: Vertical(g6,g6)
    c: Vertical(g8,g8)
    c: Vertical(g9,g9)
    c: Vertical(g10,g10)
    c: Vertical(g11,g11)
    c: Diameter(g11) = 2.5
    c: Diameter(g8) = 2.5
    c: Diameter(g9) = 2.5
    c: Diameter(g10) = 2.5
    c: Diameter(g4) = 2.5
    c: Diameter(g5) = 2.5
    c: Diameter(g6) = 2.5
    c: Diameter(g7) = 2.5
    c: Coincident(g5,g0)
    c: Coincident(g4,g5)
    c: Coincident(g6,g4)
    c: Coincident(g7,g4)
    c: Coincident(g8,g0)
    c: Coincident(g9,g8)
    c: Coincident(g10,g8)
    c: Coincident(g11,g8)
FEATURE [Part::Extrusion] Extrude005
  Base = -> Sketch005
  Dir = (0,0,1)
  DirMode = 2
  FaceMakerClass = Part::FaceMakerBullseye
  LengthFwd = 15
  LengthRev = 10
  Solid = true
  Symmetric = false
FEATURE [Part::FeaturePython] Array010  # Draft array (typed FeaturePython)
  AlwaysSyncPlacement = false
  Angle = 360
  ArrayType = 0
  Axis = (0,0,1)
  Base = -> Extrude005
  Center = (0,0,0)
  Count = 3
  ExpandArray = false
  Fuse = false
  IntervalAxis = (0,0,0)
  IntervalX = (80,0,0)
  IntervalY = (0,80,0)
  IntervalZ = (0,0,0)
  NumberCircles = 3
  NumberPolar = 5
  NumberX = 3
  NumberY = 1
  NumberZ = 1
  PlacementList = 3 placements: arithmetic series from (0,0,0) step (80,0,0) to (160,0,0)
  RadialDistance = 50
  ScaleList = (3) [(1,1,1),(1,1,1),(1,1,1)]
  Symmetry = 1
  TangentialDistance = 25
  expr: .IntervalX.x = <<Param>>.R_Grid_Across * 2
  expr: .IntervalY.y = <<Param>>.R_Grid_Along * 2
  expr: NumberX = ceil(<<Param>>.R_nof_Across / 2)
  expr: NumberY = ceil(<<Param>>.R_nof_Along / 2)
FEATURE [Sketcher::SketchObject] Sketch006
  FullyConstrained = true
  expr: Constraints[1] = <<Param>>.R_Grid_Along * (<<Param>>.R_nof_Along - 1) / 2 + <<Param>>.Heatsink_Shift
  expr: Constraints[26] = <<Param>>.R_Hole_Size
  expr: Constraints[27] = <<Param>>.R_Hole_Size
  expr: Constraints[28] = <<Param>>.R_Hole_Size
  expr: Constraints[29] = <<Param>>.R_Hole_Size
  expr: Constraints[2] = <<Param>>.Heatsink_Length / 2 - <<Param>>.R_Grid_Across * (<<Param>>.R_nof_Across - 3) / 2 - <<Param>>.R_Offset / 2
  expr: Constraints[30] = <<Param>>.R_Hole_Size
  expr: Constraints[31] = <<Param>>.R_Hole_Size
  expr: Constraints[32] = <<Param>>.R_Hole_Size
  expr: Constraints[33] = <<Param>>.R_Hole_Size
  expr: Constraints[8] = <<Param>>.R_Hole_Across
  expr: Constraints[9] = <<Param>>.R_Hole_Along
  sketch-geometry (12):
    g0: LineSegment StartX=69.4 StartY=-23.85 StartZ=0 EndX=49.6 EndY=-42.15 EndZ=0
    g1: GeomPoint X=59.5 Y=-33 Z=0
    g2: LineSegment StartX=59.5 StartY=-33 StartZ=0 EndX=69.4 EndY=-23.85 EndZ=0
    g3: LineSegment StartX=59.5 StartY=-33 StartZ=0 EndX=49.6 EndY=-42.15 EndZ=0
    g4: ArcOfCircle CenterX=69.4 CenterY=-23.85 CenterZ=0 NormalX=0 NormalY=0 NormalZ=1 AngleXU=0 Radius=1.25 StartAngle=0 EndAngle=1.5708
    g5: ArcOfCircle CenterX=69.4 CenterY=-23.85 CenterZ=0 NormalX=0 NormalY=0 NormalZ=1 AngleXU=0 Radius=1.25 StartAngle=1.5708 EndAngle=3.14159
    g6: ArcOfCircle CenterX=69.4 CenterY=-23.85 CenterZ=0 NormalX=0 NormalY=0 NormalZ=1 AngleXU=0 Radius=1.25 StartAngle=3.14159 EndAngle=4.71239
    g7: ArcOfCircle CenterX=69.4 CenterY=-23.85 CenterZ=0 NormalX=0 NormalY=0 NormalZ=1 AngleXU=0 Radius=1.25 StartAngle=4.71239 EndAngle=6.28319
    g8: ArcOfCircle CenterX=49.6 CenterY=-42.15 CenterZ=0 NormalX=0 NormalY=0 NormalZ=1 AngleXU=0 Radius=1.25 StartAngle=1e-16 EndAngle=1.5708
    g9: ArcOfCircle CenterX=49.6 CenterY=-42.15 CenterZ=0 NormalX=0 NormalY=0 NormalZ=1 AngleXU=0 Radius=1.25 StartAngle=1.5708 EndAngle=3.14159
    g10: ArcOfCircle CenterX=49.6 CenterY=-42.15 CenterZ=0 NormalX=0 NormalY=0 NormalZ=1 AngleXU=0 Radius=1.25 StartAngle=3.14159 EndAngle=4.71239
    g11: ArcOfCircle CenterX=49.6 CenterY=-42.15 CenterZ=0 NormalX=0 NormalY=0 NormalZ=1 AngleXU=0 Radius=1.25 StartAngle=4.71239 EndAngle=6.28319
  constraints (42):
    c: PointOnObject(g1,g0)
    c: Distance(g1,g-1) = 33
    c: Distance(g1,g-2) = 59.5
    c: Coincident(g2,g1)
    c: Coincident(g3,g1)
    c: Equal(g2,g3)
    c: Coincident(g3,g0)
    c: Coincident(g2,g0)
    c: DistanceX(g0,g0) = 19.8
    c: DistanceY(g0,g0) = 18.3
    c: Horizontal(g4,g4)
    c: Horizontal(g5,g5)
    c: Horizontal(g6,g6)
    c: Horizontal(g7,g7)
    c: Horizontal(g8,g8)
    c: Horizontal(g9,g9)
    c: Horizontal(g10,g10)
    c: Horizontal(g11,g11)
    c: Vertical(g8,g8)
    c: Vertical(g9,g9)
    c: Vertical(g10,g10)
    c: Vertical(g11,g11)
    c: Vertical(g4,g4)
    c: Vertical(g7,g7)
    c: Vertical(g6,g6)
    c: Vertical(g5,g5)
    c: Diameter(g4) = 2.5
    c: Diameter(g5) = 2.5
    c: Diameter(g6) = 2.5
    c: Diameter(g7) = 2.5
    c: Diameter(g8) = 2.5
    c: Diameter(g9) = 2.5
    c: Diameter(g10) = 2.5
    c: Diameter(g11) = 2.5
    c: Coincident(g8,g0)
    c: Coincident(g9,g8)
    c: Coincident(g10,g8)
    c: Coincident(g11,g8)
    c: Coincident(g5,g0)
    c: Coincident(g4,g5)
    c: Coincident(g6,g4)
    c: Coincident(g7,g4)
FEATURE [Part::Extrusion] Extrude006
  Base = -> Sketch006
  Dir = (0,0,1)
  DirMode = 2
  FaceMakerClass = Part::FaceMakerBullseye
  LengthFwd = 15
  LengthRev = 10
  Solid = true
  Symmetric = false
FEATURE [Part::FeaturePython] Array011  # Draft array (typed FeaturePython)
  AlwaysSyncPlacement = false
  Angle = 360
  ArrayType = 0
  Axis = (0,0,1)
  Base = -> Extrude006
  Center = (0,0,0)
  Count = 2
  ExpandArray = false
  Fuse = false
  IntervalAxis = (0,0,0)
  IntervalX = (80,0,0)
  IntervalY = (0,80,0)
  IntervalZ = (0,0,0)
  NumberCircles = 3
  NumberPolar = 5
  NumberX = 2
  NumberY = 1
  NumberZ = 1
  PlacementList = 2 placements: [(0,0,0),(80,0,0)]
  RadialDistance = 50
  ScaleList = (2) [(1,1,1),(1,1,1)]
  Symmetry = 1
  TangentialDistance = 25
  expr: .IntervalX.x = <<Param>>.R_Grid_Across * 2
  expr: .IntervalY.y = <<Param>>.R_Grid_Along * 2
  expr: NumberX = floor(<<Param>>.R_nof_Across / 2)
  expr: NumberY = ceil(<<Param>>.R_nof_Along / 2)
FEATURE [Sketcher::SketchObject] Sketch007
  FullyConstrained = true
  expr: Constraints[12] = <<Param>>.R_Hole_Along
  expr: Constraints[13] = <<Param>>.R_Hole_Across
  expr: Constraints[1] = <<Param>>.Heatsink_Length / 2 - <<Param>>.R_Grid_Across * (<<Param>>.R_nof_Across - 1) / 2 - <<Param>>.R_Offset / 2
  expr: Constraints[22] = <<Param>>.R_Hole_Size
  expr: Constraints[23] = <<Param>>.R_Hole_Size
  expr: Constraints[24] = <<Param>>.R_Hole_Size
  expr: Constraints[25] = <<Param>>.R_Hole_Size
  expr: Constraints[38] = <<Param>>.R_Hole_Size
  expr: Constraints[39] = <<Param>>.R_Hole_Size
  expr: Constraints[40] = <<Param>>.R_Hole_Size
  expr: Constraints[41] = <<Param>>.R_Hole_Size
  expr: Constraints[8] = <<Param>>.R_Grid_Along * (<<Param>>.R_nof_Along - 1) / 2 + <<Param>>.Heatsink_Shift
  expr: Constraints[9] = <<Param>>.R_Grid_Along
  sketch-geometry (13):
    g0: LineSegment StartX=29.4 StartY=16.15 StartZ=0 EndX=9.6 EndY=-2.15 EndZ=0
    g1: GeomPoint X=19.5 Y=7 Z=0
    g2: LineSegment StartX=19.5 StartY=7 StartZ=0 EndX=29.4 EndY=16.15 EndZ=0
    g3: LineSegment StartX=19.5 StartY=7 StartZ=0 EndX=9.6 EndY=-2.15 EndZ=0
    g4: LineSegment StartX=0 StartY=-33 StartZ=0 EndX=200 EndY=-33 EndZ=0
    g5: ArcOfCircle CenterX=29.4 CenterY=16.15 CenterZ=0 NormalX=0 NormalY=0 NormalZ=1 AngleXU=0 Radius=1.25 StartAngle=1e-16 EndAngle=1.5708
    g6: ArcOfCircle CenterX=29.4 CenterY=16.15 CenterZ=0 NormalX=0 NormalY=0 NormalZ=1 AngleXU=0 Radius=1.25 StartAngle=1.5708 EndAngle=3.14159
    g7: ArcOfCircle CenterX=29.4 CenterY=16.15 CenterZ=0 NormalX=0 NormalY=0 NormalZ=1 AngleXU=0 Radius=1.25 StartAngle=3.14159 EndAngle=4.71239
    g8: ArcOfCircle CenterX=29.4 CenterY=16.15 CenterZ=0 NormalX=0 NormalY=0 NormalZ=1 AngleXU=0 Radius=1.25 StartAngle=4.71239 EndAngle=6.28319
    g9: ArcOfCircle CenterX=9.6 CenterY=-2.15 CenterZ=0 NormalX=0 NormalY=0 NormalZ=1 AngleXU=0 Radius=1.25 StartAngle=0 EndAngle=1.5708
    g10: ArcOfCircle CenterX=9.6 CenterY=-2.15 CenterZ=0 NormalX=0 NormalY=0 NormalZ=1 AngleXU=0 Radius=1.25 StartAngle=1.5708 EndAngle=3.14159
    g11: ArcOfCircle CenterX=9.6 CenterY=-2.15 CenterZ=0 NormalX=0 NormalY=0 NormalZ=1 AngleXU=0 Radius=1.25 StartAngle=3.14159 EndAngle=4.71239
    g12: ArcOfCircle CenterX=9.6 CenterY=-2.15 CenterZ=0 NormalX=0 NormalY=0 NormalZ=1 AngleXU=0 Radius=1.25 StartAngle=4.71239 EndAngle=6.28319
  constraints (46):
    c: PointOnObject(g1,g0)
    c: Distance(g1,g-2) = 19.5
    c: Coincident(g2,g1)
    c: Coincident(g3,g1)
    c: Equal(g2,g3)
    c: PointOnObject(g4,g-2)
    c: Horizontal(g4)
    c: Distance(g4,g-2) = 200
    c: Distance(g4,g-1) = 33
    c: Distance(g1,g4) = 40
    c: Coincident(g0,g3)
    c: Coincident(g2,g0)
    c: DistanceY(g0,g0) = 18.3
    c: DistanceX(g0,g0) = 19.8
    c: Horizontal(g7,g7)
    c: Horizontal(g8,g8)
    c: Horizontal(g5,g5)
    c: Horizontal(g6,g6)
    c: Vertical(g6,g6)
    c: Vertical(g5,g5)
    c: Vertical(g8,g8)
    c: Vertical(g7,g7)
    c: Diameter(g8) = 2.5
    c: Diameter(g5) = 2.5
    c: Diameter(g6) = 2.5
    c: Diameter(g7) = 2.5
    c: Coincident(g7,g0)
    c: Coincident(g6,g7)
    c: Coincident(g5,g6)
    c: Coincident(g8,g5)
    c: Horizontal(g9,g9)
    c: Horizontal(g10,g10)
    c: Horizontal(g11,g11)
    c: Horizontal(g12,g12)
    c: Vertical(g10,g10)
    c: Vertical(g9,g9)
    c: Vertical(g12,g12)
    c: Vertical(g11,g11)
    c: Diameter(g9) = 2.5
    c: Diameter(g10) = 2.5
    c: Diameter(g11) = 2.5
    c: Diameter(g12) = 2.5
    c: Coincident(g9,g0)
    c: Coincident(g10,g9)
    c: Coincident(g11,g9)
    c: Coincident(g12,g9)
FEATURE [Part::Extrusion] Extrude007
  Base = -> Sketch007
  Dir = (0,0,1)
  DirMode = 2
  FaceMakerClass = Part::FaceMakerBullseye
  LengthFwd = 15
  LengthRev = 10
  Solid = true
  Symmetric = false
FEATURE [Part::FeaturePython] Array012  # Draft array (typed FeaturePython)
  AlwaysSyncPlacement = false
  Angle = 360
  ArrayType = 0
  Axis = (0,0,1)
  Base = -> Extrude007
  Center = (0,0,0)
  Count = 3
  ExpandArray = false
  Fuse = false
  IntervalAxis = (0,0,0)
  IntervalX = (80,0,0)
  IntervalY = (0,80,0)
  IntervalZ = (0,0,0)
  NumberCircles = 3
  NumberPolar = 5
  NumberX = 3
  NumberY = 1
  NumberZ = 1
  PlacementList = 3 placements: arithmetic series from (0,0,0) step (80,0,0) to (160,0,0)
  RadialDistance = 50
  ScaleList = (3) [(1,1,1),(1,1,1),(1,1,1)]
  Symmetry = 1
  TangentialDistance = 25
  expr: .IntervalX.x = <<Param>>.R_Grid_Across * 2
  expr: .IntervalY.y = <<Param>>.R_Grid_Along * 2
  expr: NumberX = ceil(<<Param>>.R_nof_Across / 2)
  expr: NumberY = floor(<<Param>>.R_nof_Along / 2)
FEATURE [Sketcher::SketchObject] Sketch008
  FullyConstrained = true
  expr: Constraints[10] = <<Param>>.R_Hole_Size
  expr: Constraints[11] = <<Param>>.R_Hole_Size
  expr: Constraints[12] = <<Param>>.R_Hole_Size
  expr: Constraints[13] = <<Param>>.R_Hole_Size
  expr: Constraints[16] = <<Param>>.R_Hole_Along
  expr: Constraints[17] = <<Param>>.R_Hole_Across
  expr: Constraints[1] = <<Param>>.Heatsink_Length / 2 - <<Param>>.R_Grid_Across * (<<Param>>.R_nof_Across - 3) / 2 + <<Param>>.R_Offset / 2
  expr: Constraints[38] = <<Param>>.R_Hole_Size
  expr: Constraints[39] = <<Param>>.R_Hole_Size
  expr: Constraints[40] = <<Param>>.R_Hole_Size
  expr: Constraints[41] = <<Param>>.R_Hole_Size
  expr: Constraints[8] = <<Param>>.R_Grid_Along * (<<Param>>.R_nof_Along - 1) / 2 + <<Param>>.Heatsink_Shift
  expr: Constraints[9] = <<Param>>.R_Grid_Along
  sketch-geometry (13):
    g0: LineSegment StartX=70.4 StartY=16.15 StartZ=0 EndX=50.6 EndY=-2.15 EndZ=0
    g1: GeomPoint X=60.5 Y=7 Z=0
    g2: LineSegment StartX=60.5 StartY=7 StartZ=0 EndX=70.4 EndY=16.15 EndZ=0
    g3: LineSegment StartX=60.5 StartY=7 StartZ=0 EndX=50.6 EndY=-2.15 EndZ=0
    g4: LineSegment StartX=0 StartY=-33 StartZ=0 EndX=200 EndY=-33 EndZ=0
    g5: ArcOfCircle CenterX=70.4 CenterY=16.15 CenterZ=0 NormalX=0 NormalY=0 NormalZ=1 AngleXU=0 Radius=1.25 StartAngle=0 EndAngle=1.5708
    g6: ArcOfCircle CenterX=70.4 CenterY=16.15 CenterZ=0 NormalX=0 NormalY=0 NormalZ=1 AngleXU=0 Radius=1.25 StartAngle=1.5708 EndAngle=3.14159
    g7: ArcOfCircle CenterX=70.4 CenterY=16.15 CenterZ=0 NormalX=0 NormalY=0 NormalZ=1 AngleXU=0 Radius=1.25 StartAngle=3.14159 EndAngle=4.71239
    g8: ArcOfCircle CenterX=70.4 CenterY=16.15 CenterZ=0 NormalX=0 NormalY=0 NormalZ=1 AngleXU=0 Radius=1.25 StartAngle=4.71239 EndAngle=6.28319
    g9: ArcOfCircle CenterX=50.6 CenterY=-2.15 CenterZ=0 NormalX=0 NormalY=0 NormalZ=1 AngleXU=0 Radius=1.25 StartAngle=0 EndAngle=1.5708
    g10: ArcOfCircle CenterX=50.6 CenterY=-2.15 CenterZ=0 NormalX=0 NormalY=0 NormalZ=1 AngleXU=0 Radius=1.25 StartAngle=1.5708 EndAngle=3.14159
    g11: ArcOfCircle CenterX=50.6 CenterY=-2.15 CenterZ=0 NormalX=0 NormalY=0 NormalZ=1 AngleXU=0 Radius=1.25 StartAngle=3.14159 EndAngle=4.71239
    g12: ArcOfCircle CenterX=50.6 CenterY=-2.15 CenterZ=0 NormalX=0 NormalY=0 NormalZ=1 AngleXU=0 Radius=1.25 StartAngle=4.71239 EndAngle=6.28319
  constraints (46):
    c: PointOnObject(g1,g0)
    c: Distance(g1,g-2) = 60.5
    c: Coincident(g2,g1)
    c: Coincident(g3,g1)
    c: Equal(g2,g3)
    c: PointOnObject(g4,g-2)
    c: Horizontal(g4)
    c: Distance(g4,g-2) = 200
    c: Distance(g4,g-1) = 33
    c: Distance(g1,g4) = 40
    c: Diameter(g5) = 2.5
    c: Diameter(g6) = 2.5
    c: Diameter(g7) = 2.5
    c: Diameter(g8) = 2.5
    c: Coincident(g2,g0)
    c: Coincident(g0,g3)
    c: DistanceY(g0,g0) = 18.3
    c: DistanceX(g0,g0) = 19.8
    c: Horizontal(g7,g7)
    c: Horizontal(g6,g6)
    c: Horizontal(g5,g5)
    c: Horizontal(g8,g8)
    c: Vertical(g6,g6)
    c: Vertical(g5,g5)
    c: Vertical(g8,g8)
    c: Vertical(g7,g7)
    c: Coincident(g6,g0)
    c: Coincident(g5,g6)
    c: Coincident(g8,g5)
    c: Coincident(g7,g5)
    c: Horizontal(g11,g11)
    c: Horizontal(g10,g10)
    c: Horizontal(g9,g9)
    c: Horizontal(g12,g12)
    c: Vertical(g10,g10)
    c: Vertical(g9,g9)
    c: Vertical(g12,g12)
    c: Vertical(g11,g11)
    c: Diameter(g12) = 2.5
    c: Diameter(g9) = 2.5
    c: Diameter(g10) = 2.5
    c: Diameter(g11) = 2.5
    c: Coincident(g10,g0)
    c: Coincident(g9,g10)
    c: Coincident(g12,g9)
    c: Coincident(g11,g9)
FEATURE [Part::Extrusion] Extrude008
  Base = -> Sketch008
  Dir = (0,0,1)
  DirMode = 2
  FaceMakerClass = Part::FaceMakerBullseye
  LengthFwd = 15
  LengthRev = 10
  Solid = true
  Symmetric = false
FEATURE [Part::FeaturePython] Array013  # Draft array (typed FeaturePython)
  AlwaysSyncPlacement = false
  Angle = 360
  ArrayType = 0
  Axis = (0,0,1)
  Base = -> Extrude008
  Center = (0,0,0)
  Count = 2
  ExpandArray = false
  Fuse = false
  IntervalAxis = (0,0,0)
  IntervalX = (80,0,0)
  IntervalY = (0,80,0)
  IntervalZ = (0,0,0)
  NumberCircles = 3
  NumberPolar = 5
  NumberX = 2
  NumberY = 1
  NumberZ = 1
  PlacementList = 2 placements: [(0,0,0),(80,0,0)]
  RadialDistance = 50
  ScaleList = (2) [(1,1,1),(1,1,1)]
  Symmetry = 1
  TangentialDistance = 25
  expr: .IntervalX.x = <<Param>>.R_Grid_Across * 2
  expr: .IntervalY.y = <<Param>>.R_Grid_Along * 2
  expr: NumberX = floor(<<Param>>.R_nof_Across / 2)
  expr: NumberY = floor(<<Param>>.R_nof_Along / 2)
FEATURE [Part::MultiFuse] Fusion002
  Shapes = -> [Array010,Array011,Array012,Array013]
FEATURE [Sketcher::SketchObject] Sketch009
  FullyConstrained = true
  expr: Constraints[12] = <<Param>>.Heatsink_Thread_Hole
  expr: Constraints[13] = <<Param>>.Heatsink_Thread_Hole
  expr: Constraints[14] = <<Param>>.Heatsink_Thread_Hole
  expr: Constraints[15] = <<Param>>.Heatsink_Thread_Hole
  expr: Constraints[19] = <<Param>>.Heatsink_Hole_Grid_y * (<<Param>>.Heatsink_Hole_nof_y - 1) / 2 + <<Param>>.Heatsink_Shift
  expr: Constraints[20] = <<Param>>.Heatsink_Hole_Grid_x * (<<Param>>.Heatsink_Hole_nof_x - 1) / 2
  expr: Constraints[3] = <<Param>>.Heatsink_Length / 2
  sketch-geometry (5):
    g0: LineSegment StartX=100 StartY=0 StartZ=0 EndX=100 EndY=-100 EndZ=0
    g1: ArcOfCircle CenterX=10 CenterY=-58 CenterZ=0 NormalX=0 NormalY=0 NormalZ=1 AngleXU=0 Radius=1.25 StartAngle=0 EndAngle=1.5708
    g2: ArcOfCircle CenterX=10 CenterY=-58 CenterZ=0 NormalX=0 NormalY=0 NormalZ=1 AngleXU=0 Radius=1.25 StartAngle=1.5708 EndAngle=3.14159
    g3: ArcOfCircle CenterX=10 CenterY=-58 CenterZ=0 NormalX=0 NormalY=0 NormalZ=1 AngleXU=0 Radius=1.25 StartAngle=3.14159 EndAngle=4.71239
    g4: ArcOfCircle CenterX=10 CenterY=-58 CenterZ=0 NormalX=0 NormalY=0 NormalZ=1 AngleXU=0 Radius=1.25 StartAngle=4.71239 EndAngle=6.28319
  constraints (21):
    c: PointOnObject(g0,g-1)
    c: Vertical(g0)
    c: Distance(g0) = 100
    c: Distance(g0,g-2) = 100
    c: Horizontal(g4,g4)
    c: Horizontal(g1,g1)
    c: Horizontal(g2,g2)
    c: Horizontal(g3,g3)
    c: Vertical(g3,g3)
    c: Vertical(g4,g4)
    c: Vertical(g1,g1)
    c: Vertical(g2,g2)
    c: Diameter(g1) = 2.5
    c: Diameter(g4) = 2.5
    c: Diameter(g3) = 2.5
    c: Diameter(g2) = 2.5
    c: Coincident(g1,g2)
    c: Coincident(g1,g4)
    c: Coincident(g1,g3)
    c: Distance(g1,g-1) = 58
    c: Distance(g1,g0) = 90
FEATURE [PartDesign::CoordinateSystem] LCS_Origin
  AttacherType = Attacher::AttachEngine3D
  MapMode = 2
  Support = -> [X_Axis001]
FEATURE [App::DocumentObjectGroup] Constraints
FEATURE [Part::Feature] Part__Feature  label="1599K Lid"
  Placement = pos=(-35.5062,-49.1401,-2.40297) rot=(1,0,0;3.14159rad)
  shape: bbox 220 x 140 x 522.1 mm, 504 faces (baked)
FEATURE [Part::Feature] Part__Feature001  label="1599K Box"
  Placement = pos=(-35.5062,-49.1401,-3.40297) rot=(0,0,1;0rad)
  shape: bbox 220 x 140 x 525.6 mm, 228 faces (baked)
FEATURE [Part::Feature] Part__Feature002  label="SC590 (screw M3-0.5X 12mm FH)"
  Placement = pos=(-134.506,9.85994,4.35203) rot=(1,0,0;1.5708rad)
  shape: bbox 5.514 x 5.514 x 12.01 mm, 26 faces (baked)
FEATURE [Part::Feature] Part__Feature003  label="SC590 (screw M3-0.5X 12mm FH)001"
  Placement = pos=(-134.506,-108.14,4.35203) rot=(1,0,0;1.5708rad)
  shape: bbox 5.514 x 5.514 x 12.01 mm, 26 faces (baked)
FEATURE [Part::Feature] Part__Feature004  label="SC590 (screw M3-0.5X 12mm FH)002"
  Placement = pos=(63.4938,9.85994,4.35203) rot=(0.97539,-0.155908,-0.155908;1.59571rad)
  shape: bbox 5.514 x 5.514 x 12.01 mm, 26 faces (baked)
FEATURE [Part::Feature] Part__Feature005  label="SC590 (screw M3-0.5X 12mm FH)003"
  Placement = pos=(63.4938,-108.14,4.35203) rot=(1,0,0;1.5708rad)
  shape: bbox 5.514 x 5.514 x 12.01 mm, 26 faces (baked)
FEATURE [Part::Feature] Part__Feature006  label="IN100 (insert M3-0.5X5.75mm BRASS)"
  Placement = pos=(63.4938,9.85994,-6.61797) rot=(1,0,0;1.5708rad)
  shape: bbox 4.846 x 4.846 x 5.715 mm, 136 faces (baked)
FEATURE [Part::Feature] Part__Feature007  label="IN100 (insert M3-0.5X5.75mm BRASS)001"
  Placement = pos=(-134.506,9.85994,-6.61797) rot=(1,0,0;1.5708rad)
  shape: bbox 4.846 x 4.846 x 5.715 mm, 136 faces (baked)
FEATURE [Part::Feature] Part__Feature008  label="IN100 (insert M3-0.5X5.75mm BRASS)002"
  Placement = pos=(63.4938,-108.14,-6.61797) rot=(1,0,0;1.5708rad)
  shape: bbox 4.846 x 4.846 x 5.715 mm, 136 faces (baked)
FEATURE [Part::Feature] Part__Feature009  label="IN100 (insert M3-0.5X5.75mm BRASS)003"
  Placement = pos=(-134.506,-108.14,-6.61797) rot=(1,0,0;1.5708rad)
  shape: bbox 4.846 x 4.846 x 5.715 mm, 136 faces (baked)
FEATURE [App::Part] _599K  label="1599K"
  Group = -> [Part__Feature,Part__Feature001,Part__Feature002,Part__Feature003,Part__Feature004,Part__Feature005,Part__Feature006,Part__Feature007,Part__Feature008,Part__Feature009]
  Origin = -> Origin
  Placement = pos=(135,-49.14,-32.403) rot=(1,0,0;3.14159rad)
FEATURE [Part::Feature] Part__Feature011  label="10021079"
  Placement = pos=(5,48,-21) rot=(0,0,1;0rad)
  shape: bbox 15.72 x 15.72 x 32.42 mm, 532 faces, 2 solids (baked)
  expr: .Placement.Base.x = <<Param>>.Heatsink_Length / 2 - <<Param>>.Con_Grid * (<<Param>>.Con_nof - 1) / 2
  expr: .Placement.Base.y = <<Param>>.Con_Pos_y
FEATURE [Part::FeaturePython] Array  label="Connectors"  # Draft array (typed FeaturePython)
  Angle = 360
  ArrayType = 0
  Axis = (0,0,1)
  Base = -> Part__Feature011
  Center = (0,0,0)
  Fuse = false
  IntervalAxis = (0,0,0)
  IntervalX = (19,0,0)
  IntervalY = (0,-100,0)
  IntervalZ = (0,0,1)
  NumberPolar = 1
  NumberX = 11
  NumberY = 1
  NumberZ = 1
  expr: .IntervalX.x = <<Param>>.Con_Grid
FEATURE [Part::Feature] Part__Feature010  label="SK047"
  Placement = pos=(0,0,0) rot=(1,0,0;1.5708rad)
  shape: bbox 200 x 10 x 40 mm, 124 faces (baked)
FEATURE [Part::FeaturePython] Scale001  label="SK47-100"  # Draft clone (typed FeaturePython)
  AssemblyType = Part::Link
  AttachedBy = Origin
  AttachedTo = Parent Assembly#LCS_Origin
  AttachmentOffset = pos=(0,37,0) rot=(1,0,0;1.5708rad)
  Fuse = false
  Objects = -> [Part__Feature010]
  Placement = pos=(0,37,0) rot=(1,0,0;1.5708rad)
  Scale = (1,1,10)
  SolverId = Asm4EE
  expr: Placement = LCS_Origin.Placement * AttachmentOffset
FEATURE [App::DocumentObjectGroup] Configurations
FEATURE [App::FeaturePython] Variables  # WARN: FeaturePython — macro-defined, semantics opaque (R4)
  Type = App::PropertyContainer
FEATURE [App::Part] Model
  AssemblyType = Part::Link
  Group = -> [LCS_Origin,Constraints,Variables,Configurations,Scale001,_599K,Part__Feature011,Array,Part__Feature010]
  Origin = -> Origin001
  Type = Assembly
FEATURE [Sketcher::SketchObject] Sketch010
  FullyConstrained = true
  expr: Constraints[0] = <<Param>>.Heatsink_Hole
  expr: Constraints[1] = <<Param>>.Heatsink_Hole_Grid_y * (<<Param>>.Heatsink_Hole_nof_y - 1) / 2 + <<Param>>.Heatsink_Shift
  expr: Constraints[5] = <<Param>>.Heatsink_Hole_Grid_x * (<<Param>>.Heatsink_Hole_nof_x - 1) / 2
  expr: Constraints[6] = <<Param>>.Heatsink_Length / 2
  sketch-geometry (2):
    g0: Circle CenterX=10 CenterY=-58 CenterZ=0 NormalX=0 NormalY=0 NormalZ=1 AngleXU=0 Radius=1.6
    g1: LineSegment StartX=100 StartY=0 StartZ=0 EndX=100 EndY=-100 EndZ=0
  constraints (7):
    c: Diameter(g0) = 3.2
    c: Distance(g0,g-1) = 58
    c: PointOnObject(g1,g-1)
    c: Vertical(g1)
    c: Distance(g1) = 100
    c: Distance(g0,g1) = 90
    c: Distance(g1,g-2) = 100
FEATURE [Part::Extrusion] Extrude010
  Base = -> Sketch010
  Dir = (0,0,1)
  DirMode = 2
  FaceMakerClass = Part::FaceMakerBullseye
  LengthFwd = 15
  LengthRev = 10
  Solid = true
  Symmetric = false
FEATURE [Part::FeaturePython] Array015  # Draft array (typed FeaturePython)
  AlwaysSyncPlacement = false
  Angle = 360
  ArrayType = 0
  Axis = (0,0,1)
  Base = -> Extrude010
  Center = (0,0,0)
  Count = 12
  ExpandArray = false
  Fuse = false
  IntervalAxis = (0,0,0)
  IntervalX = (60,0,0)
  IntervalY = (0,45,0)
  IntervalZ = (0,0,100)
  NumberCircles = 3
  NumberPolar = 5
  NumberX = 4
  NumberY = 3
  NumberZ = 1
  PlacementList = 12 placements: [(0,0,0),(0,45,0),(0,90,0),(60,0,0),(60,45,0),(60,90,0),(120,0,0),(120,45,0),(120,90,0),(180,0,0),(180,45,0),(180,90,0)]
  RadialDistance = 50
  ScaleList = (12) [(1,1,1),(1,1,1),(1,1,1),(1,1,1),(1,1,1),(1,1,1),(1,1,1),(1,1,1),(1,1,1),(1,1,1),(1,1,1),(1,1,1)]
  Symmetry = 1
  TangentialDistance = 25
  expr: .IntervalX.x = <<Param>>.Heatsink_Hole_Grid_x
  expr: .IntervalY.y = <<Param>>.Heatsink_Hole_Grid_y
  expr: NumberX = <<Param>>.Heatsink_Hole_nof_x
  expr: NumberY = <<Param>>.Heatsink_Hole_nof_y
FEATURE [Part::MultiFuse] Fusion004
  Shapes = -> [Array015,Fusion001]
FEATURE [Part::Cut] Cut  label="Housing_milled"
  Base = -> _599K
  Tool = -> Fusion004
FEATURE [TechDraw::DrawSVGTemplate] Template
  EditableTexts = AuthorName=AUTHOR NAME,CheckDate=CHECK DATE,CreationDate=CREATION DATE,DrawingNumber=NUMBER,FC-Scale=SCALE,FC-Title=TITLE,SheetNumber=SHEET,+3 more (map truncated)
  Height = 297
  Orientation = 1
  Width = 420
FEATURE [TechDraw::DrawProjGroupItem] ProjItem  label="Front"
  CoarseView = false
  Direction = (0,0,1)
  Focus = 100
  HardHidden = false
  IsoCount = 0
  IsoHidden = false
  IsoVisible = false
  LockPosition = true
  Perspective = false
  Rotation = 0
  RotationVector = (1,0,0)
  ScaleType = 2
  SeamHidden = false
  SeamVisible = true
  SmoothHidden = false
  SmoothVisible = true
  Source = -> [Cut]
  Type = 0
  X = 0
  XDirection = (1,0,0)
  Y = 0
FEATURE [TechDraw::DrawProjGroup] ProjGroup
  Anchor = -> ProjItem
  AutoDistribute = true
  LockPosition = false
  ProjectionType = 0
  Rotation = 0
  ScaleType = 0
  Source = -> [Cut]
  Views = -> [ProjItem]
  X = 202.798
  Y = 171.305
  spacingX = 15
  spacingY = 15
FEATURE [TechDraw::DrawPage] Page  label="Drawing_Housing"
  KeepUpdated = true
  NextBalloonIndex = 1
  ProjectionType = 0
  Template = -> Template
  Views = -> [ProjGroup]
FEATURE [Part::Extrusion] Extrude011
  Base = -> Sketch009
  Dir = (0,0,1)
  DirMode = 2
  FaceMakerClass = Part::FaceMakerBullseye
  LengthFwd = 15
  LengthRev = 10
  Solid = true
  Symmetric = false
FEATURE [Part::FeaturePython] Array016  # Draft array (typed FeaturePython)
  AlwaysSyncPlacement = false
  Angle = 360
  ArrayType = 0
  Axis = (0,0,1)
  Base = -> Extrude011
  Center = (0,0,0)
  Count = 12
  ExpandArray = false
  Fuse = false
  IntervalAxis = (0,0,0)
  IntervalX = (60,0,0)
  IntervalY = (0,45,0)
  IntervalZ = (0,0,100)
  NumberCircles = 3
  NumberPolar = 5
  NumberX = 4
  NumberY = 3
  NumberZ = 1
  PlacementList = 12 placements: [(0,0,0),(0,45,0),(0,90,0),(60,0,0),(60,45,0),(60,90,0),(120,0,0),(120,45,0),(120,90,0),(180,0,0),(180,45,0),(180,90,0)]
  RadialDistance = 50
  ScaleList = (12) [(1,1,1),(1,1,1),(1,1,1),(1,1,1),(1,1,1),(1,1,1),(1,1,1),(1,1,1),(1,1,1),(1,1,1),(1,1,1),(1,1,1)]
  Symmetry = 1
  TangentialDistance = 25
  expr: .IntervalX.x = <<Param>>.Heatsink_Hole_Grid_x
  expr: .IntervalY.y = <<Param>>.Heatsink_Hole_Grid_y
  expr: NumberX = <<Param>>.Heatsink_Hole_nof_x
  expr: NumberY = <<Param>>.Heatsink_Hole_nof_y
FEATURE [Part::MultiFuse] Fusion005
  Shapes = -> [Fusion002,Array016]
FEATURE [Part::Cut] Cut001  label="Heatsink_drilled"
  Base = -> Scale001
  Tool = -> Fusion005
FEATURE [TechDraw::DrawSVGTemplate] Template001
  EditableTexts = AuthorName=AUTHOR NAME,CheckDate=CHECK DATE,CreationDate=CREATION DATE,DrawingNumber=NUMBER,FC-Scale=SCALE,FC-Title=TITLE,SheetNumber=SHEET,+3 more (map truncated)
  Height = 297
  Orientation = 1
  Width = 420
FEATURE [TechDraw::DrawProjGroupItem] ProjItem001  label="Front001"
  CoarseView = false
  Direction = (0,0,-1)
  Focus = 100
  HardHidden = false
  IsoCount = 0
  IsoHidden = false
  IsoVisible = false
  LockPosition = true
  Perspective = false
  Rotation = 0
  RotationVector = (1,0,0)
  ScaleType = 2
  SeamHidden = false
  SeamVisible = true
  SmoothHidden = false
  SmoothVisible = true
  Source = -> [Cut001]
  Type = 0
  X = 0
  XDirection = (1,0,0)
  Y = 0
FEATURE [TechDraw::DrawProjGroup] ProjGroup001
  Anchor = -> ProjItem001
  AutoDistribute = true
  LockPosition = false
  ProjectionType = 0
  Rotation = 0
  ScaleType = 0
  Source = -> [Cut001]
  Views = -> [ProjItem001]
  X = 230.749
  Y = 197.111
  spacingX = 15
  spacingY = 15
FEATURE [TechDraw::DrawViewDimension] Dimension
  AngleOverride = false
  Arbitrary = false
  ArbitraryTolerances = false
  EqualTolerance = true
  ExtensionAngle = 0
  FormatSpec = %.2w
  FormatSpecOverTolerance = %+.2w
  FormatSpecUnderTolerance = %+.2w
  Inverted = false
  LineAngle = 0
  LockPosition = false
  MeasureType = 1
  OverTolerance = 0
  References2D = -> [ProjItem001]
  Rotation = 0
  ScaleType = 0
  TheoreticalExact = false
  Type = 1
  UnderTolerance = 0
  X = 0.702415
  Y = 62.7355
FEATURE [TechDraw::DrawViewDimension] Dimension001
  AngleOverride = false
  Arbitrary = false
  ArbitraryTolerances = false
  EqualTolerance = true
  ExtensionAngle = 0
  FormatSpec = %.2w
  FormatSpecOverTolerance = %+.2w
  FormatSpecUnderTolerance = %+.2w
  Inverted = false
  LineAngle = 0
  LockPosition = false
  MeasureType = 1
  OverTolerance = 0
  References2D = -> [ProjItem001]
  Rotation = 0
  ScaleType = 0
  TheoreticalExact = false
  Type = 2
  UnderTolerance = 0
  X = 117.258
  Y = 2.02744
FEATURE [TechDraw::DrawViewDimension] Dimension002
  AngleOverride = false
  Arbitrary = false
  ArbitraryTolerances = false
  EqualTolerance = true
  ExtensionAngle = 0
  FormatSpec = %.2w
  FormatSpecOverTolerance = %+.2w
  FormatSpecUnderTolerance = %+.2w
  Inverted = false
  LineAngle = 0
  LockPosition = false
  MeasureType = 1
  OverTolerance = 0
  References2D = -> [ProjItem001]
  Rotation = 0
  ScaleType = 0
  TheoreticalExact = false
  Type = 1
  UnderTolerance = 0
  X = -95
  Y = -53.523
FEATURE [TechDraw::DrawViewDimension] Dimension003
  AngleOverride = false
  Arbitrary = false
  ArbitraryTolerances = false
  EqualTolerance = true
  ExtensionAngle = 0
  FormatSpec = %.2w
  FormatSpecOverTolerance = %+.2w
  FormatSpecUnderTolerance = %+.2w
  Inverted = false
  LineAngle = 0
  LockPosition = false
  MeasureType = 1
  OverTolerance = 0
  References2D = -> [ProjItem001]
  Rotation = 0
  ScaleType = 0
  TheoreticalExact = false
  Type = 1
  UnderTolerance = 0
  X = -41.0842
  Y = -53.6139
FEATURE [TechDraw::DrawViewDimension] Dimension004
  AngleOverride = false
  Arbitrary = false
  ArbitraryTolerances = false
  EqualTolerance = true
  ExtensionAngle = 0
  FormatSpec = %.2w
  FormatSpecOverTolerance = %+.2w
  FormatSpecUnderTolerance = %+.2w
  Inverted = false
  LineAngle = 0
  LockPosition = false
  MeasureType = 1
  OverTolerance = 0
  References2D = -> [ProjItem001]
  Rotation = 0
  ScaleType = 0
  TheoreticalExact = false
  Type = 1
  UnderTolerance = 0
  X = 21.6008
  Y = -53.7049
FEATURE [TechDraw::DrawViewDimension] Dimension005
  AngleOverride = false
  Arbitrary = false
  ArbitraryTolerances = false
  EqualTolerance = true
  ExtensionAngle = 0
  FormatSpec = %.2w
  FormatSpecOverTolerance = %+.2w
  FormatSpecUnderTolerance = %+.2w
  Inverted = false
  LineAngle = 0
  LockPosition = false
  MeasureType = 1
  OverTolerance = 0
  References2D = -> [ProjItem001]
  Rotation = 0
  ScaleType = 0
  TheoreticalExact = false
  Type = 1
  UnderTolerance = 0
  X = 82.1599
  Y = -53.7959
FEATURE [TechDraw::DrawViewDimension] Dimension006
  AngleOverride = false
  Arbitrary = false
  ArbitraryTolerances = false
  EqualTolerance = true
  ExtensionAngle = 0
  FormatSpec = %.2w
  FormatSpecOverTolerance = %+.2w
  FormatSpecUnderTolerance = %+.2w
  Inverted = false
  LineAngle = 0
  LockPosition = false
  MeasureType = 1
  OverTolerance = 0
  References2D = -> [ProjItem001]
  Rotation = 0
  ScaleType = 0
  TheoreticalExact = false
  Type = 1
  UnderTolerance = 0
  X = -94.2641
  Y = -14.1978
FEATURE [TechDraw::DrawViewDimension] Dimension007
  AngleOverride = false
  Arbitrary = false
  ArbitraryTolerances = false
  EqualTolerance = true
  ExtensionAngle = 0
  FormatSpec = %.2w
  FormatSpecOverTolerance = %+.2w
  FormatSpecUnderTolerance = %+.2w
  Inverted = false
  LineAngle = 0
  LockPosition = false
  MeasureType = 1
  OverTolerance = 0
  References2D = -> [ProjItem001]
  Rotation = 0
  ScaleType = 0
  TheoreticalExact = false
  Type = 1
  UnderTolerance = 0
  X = -76.7602
  Y = -30.7178
FEATURE [TechDraw::DrawViewDimension] Dimension008
  AngleOverride = false
  Arbitrary = false
  ArbitraryTolerances = false
  EqualTolerance = true
  ExtensionAngle = 0
  FormatSpec = %.2w
  FormatSpecOverTolerance = %+.2w
  FormatSpecUnderTolerance = %+.2w
  Inverted = false
  LineAngle = 0
  LockPosition = false
  MeasureType = 1
  OverTolerance = 0
  References2D = -> [ProjItem001]
  Rotation = 0
  ScaleType = 0
  TheoreticalExact = false
  Type = 1
  UnderTolerance = 0
  X = -55.6316
  Y = -14.0808
FEATURE [TechDraw::DrawViewDimension] Dimension009
  AngleOverride = false
  Arbitrary = false
  ArbitraryTolerances = false
  EqualTolerance = true
  ExtensionAngle = 0
  FormatSpec = %.2w
  FormatSpecOverTolerance = %+.2w
  FormatSpecUnderTolerance = %+.2w
  Inverted = false
  LineAngle = 0
  LockPosition = false
  MeasureType = 1
  OverTolerance = 0
  References2D = -> [ProjItem001]
  Rotation = 0
  ScaleType = 0
  TheoreticalExact = false
  Type = 1
  UnderTolerance = 0
  X = -36.4898
  Y = -30.8348
FEATURE [TechDraw::DrawViewDimension] Dimension010
  AngleOverride = false
  Arbitrary = false
  ArbitraryTolerances = false
  EqualTolerance = true
  ExtensionAngle = 0
  FormatSpec = %.2w
  FormatSpecOverTolerance = %+.2w
  FormatSpecUnderTolerance = %+.2w
  Inverted = false
  LineAngle = 0
  LockPosition = false
  MeasureType = 1
  OverTolerance = 0
  References2D = -> [ProjItem001]
  Rotation = 0
  ScaleType = 0
  TheoreticalExact = false
  Type = 1
  UnderTolerance = 0
  X = -18.467
  Y = -14.1978
FEATURE [TechDraw::DrawViewDimension] Dimension011
  AngleOverride = false
  Arbitrary = false
  ArbitraryTolerances = false
  EqualTolerance = true
  ExtensionAngle = 0
  FormatSpec = %.2w
  FormatSpecOverTolerance = %+.2w
  FormatSpecUnderTolerance = %+.2w
  Inverted = false
  LineAngle = 0
  LockPosition = false
  MeasureType = 1
  OverTolerance = 0
  References2D = -> [ProjItem001]
  Rotation = 0
  ScaleType = 0
  TheoreticalExact = false
  Type = 1
  UnderTolerance = 0
  X = 1.5311
  Y = -30.8909
FEATURE [TechDraw::DrawViewDimension] Dimension012
  AngleOverride = false
  Arbitrary = false
  ArbitraryTolerances = false
  EqualTolerance = true
  ExtensionAngle = 0
  FormatSpec = %.2w
  FormatSpecOverTolerance = %+.2w
  FormatSpecUnderTolerance = %+.2w
  Inverted = false
  LineAngle = 0
  LockPosition = false
  MeasureType = 1
  OverTolerance = 0
  References2D = -> [ProjItem001]
  Rotation = 0
  ScaleType = 0
  TheoreticalExact = false
  Type = 1
  UnderTolerance = 0
  X = 24.0916
  Y = -14.1603
FEATURE [TechDraw::DrawViewDimension] Dimension013
  AngleOverride = false
  Arbitrary = false
  ArbitraryTolerances = false
  EqualTolerance = true
  ExtensionAngle = 0
  FormatSpec = %.2w
  FormatSpecOverTolerance = %+.2w
  FormatSpecUnderTolerance = %+.2w
  Inverted = false
  LineAngle = 0
  LockPosition = false
  MeasureType = 1
  OverTolerance = 0
  References2D = -> [ProjItem001]
  Rotation = 0
  ScaleType = 0
  TheoreticalExact = false
  Type = 1
  UnderTolerance = 0
  X = 43.4252
  Y = -30.8909
FEATURE [TechDraw::DrawViewDimension] Dimension014
  AngleOverride = false
  Arbitrary = false
  ArbitraryTolerances = false
  EqualTolerance = true
  ExtensionAngle = 0
  FormatSpec = %.2w
  FormatSpecOverTolerance = %+.2w
  FormatSpecUnderTolerance = %+.2w
  Inverted = false
  LineAngle = 0
  LockPosition = false
  MeasureType = 1
  OverTolerance = 0
  References2D = -> [ProjItem001]
  Rotation = 0
  ScaleType = 0
  TheoreticalExact = false
  Type = 1
  UnderTolerance = 0
  X = 61.2796
  Y = -14.1603
FEATURE [TechDraw::DrawViewDimension] Dimension015
  AngleOverride = false
  Arbitrary = false
  ArbitraryTolerances = false
  EqualTolerance = true
  ExtensionAngle = 0
  FormatSpec = %.2w
  FormatSpecOverTolerance = %+.2w
  FormatSpecUnderTolerance = %+.2w
  Inverted = false
  LineAngle = 0
  LockPosition = false
  MeasureType = 1
  OverTolerance = 0
  References2D = -> [ProjItem001]
  Rotation = 0
  ScaleType = 0
  TheoreticalExact = false
  Type = 1
  UnderTolerance = 0
  X = 82.1293
  Y = -30.8909
FEATURE [TechDraw::DrawViewDimension] Dimension016
  AngleOverride = false
  Arbitrary = false
  ArbitraryTolerances = false
  EqualTolerance = true
  ExtensionAngle = 0
  FormatSpec = %.2w
  FormatSpecOverTolerance = %+.2w
  FormatSpecUnderTolerance = %+.2w
  Inverted = false
  LineAngle = 0
  LockPosition = false
  MeasureType = 1
  OverTolerance = 0
  References2D = -> [ProjItem001]
  Rotation = 0
  ScaleType = 0
  TheoreticalExact = false
  Type = 1
  UnderTolerance = 0
  X = -93.9619
  Y = 26.47
FEATURE [TechDraw::DrawViewDimension] Dimension017
  AngleOverride = false
  Arbitrary = false
  ArbitraryTolerances = false
  EqualTolerance = true
  ExtensionAngle = 0
  FormatSpec = %.2w
  FormatSpecOverTolerance = %+.2w
  FormatSpecUnderTolerance = %+.2w
  Inverted = false
  LineAngle = 0
  LockPosition = false
  MeasureType = 1
  OverTolerance = 0
  References2D = -> [ProjItem001]
  Rotation = 0
  ScaleType = 0
  TheoreticalExact = false
  Type = 1
  UnderTolerance = 0
  X = -75.7578
  Y = 9.93859
FEATURE [TechDraw::DrawViewDimension] Dimension018
  AngleOverride = false
  Arbitrary = false
  ArbitraryTolerances = false
  EqualTolerance = true
  ExtensionAngle = 0
  FormatSpec = %.2w
  FormatSpecOverTolerance = %+.2w
  FormatSpecUnderTolerance = %+.2w
  Inverted = false
  LineAngle = 0
  LockPosition = false
  MeasureType = 1
  OverTolerance = 0
  References2D = -> [ProjItem001]
  Rotation = 0
  ScaleType = 0
  TheoreticalExact = false
  Type = 1
  UnderTolerance = 0
  X = -56.7464
  Y = 26.47
FEATURE [TechDraw::DrawViewDimension] Dimension019
  AngleOverride = false
  Arbitrary = false
  ArbitraryTolerances = false
  EqualTolerance = true
  ExtensionAngle = 0
  FormatSpec = %.2w
  FormatSpecOverTolerance = %+.2w
  FormatSpecUnderTolerance = %+.2w
  Inverted = false
  LineAngle = 0
  LockPosition = false
  MeasureType = 1
  OverTolerance = 0
  References2D = -> [ProjItem001]
  Rotation = 0
  ScaleType = 0
  TheoreticalExact = false
  Type = 1
  UnderTolerance = 0
  X = -37.9887
  Y = 10.1231
FEATURE [TechDraw::DrawViewDimension] Dimension020
  AngleOverride = false
  Arbitrary = false
  ArbitraryTolerances = false
  EqualTolerance = true
  ExtensionAngle = 0
  FormatSpec = %.2w
  FormatSpecOverTolerance = %+.2w
  FormatSpecUnderTolerance = %+.2w
  Inverted = false
  LineAngle = 0
  LockPosition = false
  MeasureType = 1
  OverTolerance = 0
  References2D = -> [ProjItem001]
  Rotation = 0
  ScaleType = 0
  TheoreticalExact = false
  Type = 1
  UnderTolerance = 0
  X = -15.3939
  Y = 26.47
FEATURE [TechDraw::DrawViewDimension] Dimension021
  AngleOverride = false
  Arbitrary = false
  ArbitraryTolerances = false
  EqualTolerance = true
  ExtensionAngle = 0
  FormatSpec = %.2w
  FormatSpecOverTolerance = %+.2w
  FormatSpecUnderTolerance = %+.2w
  Inverted = false
  LineAngle = 0
  LockPosition = false
  MeasureType = 1
  OverTolerance = 0
  References2D = -> [ProjItem001]
  Rotation = 0
  ScaleType = 0
  TheoreticalExact = false
  Type = 1
  UnderTolerance = 0
  X = 3.73287
  Y = 10.1231
FEATURE [TechDraw::DrawViewDimension] Dimension022
  AngleOverride = false
  Arbitrary = false
  ArbitraryTolerances = false
  EqualTolerance = true
  ExtensionAngle = 0
  FormatSpec = %.2w
  FormatSpecOverTolerance = %+.2w
  FormatSpecUnderTolerance = %+.2w
  Inverted = false
  LineAngle = 0
  LockPosition = false
  MeasureType = 1
  OverTolerance = 0
  References2D = -> [ProjItem001]
  Rotation = 0
  ScaleType = 0
  TheoreticalExact = false
  Type = 1
  UnderTolerance = 0
  X = 22.006
  Y = 26.47
FEATURE [TechDraw::DrawViewDimension] Dimension024
  AngleOverride = false
  Arbitrary = false
  ArbitraryTolerances = false
  EqualTolerance = true
  ExtensionAngle = 0
  FormatSpec = %.2w
  FormatSpecOverTolerance = %+.2w
  FormatSpecUnderTolerance = %+.2w
  Inverted = false
  LineAngle = 0
  LockPosition = false
  MeasureType = 1
  OverTolerance = 0
  References2D = -> [ProjItem001]
  Rotation = 0
  ScaleType = 0
  TheoreticalExact = false
  Type = 1
  UnderTolerance = 0
  X = 41.871
  Y = 9.98034
FEATURE [TechDraw::DrawViewDimension] Dimension025
  AngleOverride = false
  Arbitrary = false
  ArbitraryTolerances = false
  EqualTolerance = true
  ExtensionAngle = 0
  FormatSpec = %.2w
  FormatSpecOverTolerance = %+.2w
  FormatSpecUnderTolerance = %+.2w
  Inverted = false
  LineAngle = 0
  LockPosition = false
  MeasureType = 1
  OverTolerance = 0
  References2D = -> [ProjItem001]
  Rotation = 0
  ScaleType = 0
  TheoreticalExact = false
  Type = 1
  UnderTolerance = 0
  X = 64.2812
  Y = 26.47
FEATURE [TechDraw::DrawViewDimension] Dimension026
  AngleOverride = false
  Arbitrary = false
  ArbitraryTolerances = false
  EqualTolerance = true
  ExtensionAngle = 0
  FormatSpec = %.2w
  FormatSpecOverTolerance = %+.2w
  FormatSpecUnderTolerance = %+.2w
  Inverted = false
  LineAngle = 0
  LockPosition = false
  MeasureType = 1
  OverTolerance = 0
  References2D = -> [ProjItem001]
  Rotation = 0
  ScaleType = 0
  TheoreticalExact = false
  Type = 1
  UnderTolerance = 0
  X = 83.408
  Y = 10.1649
FEATURE [TechDraw::DrawViewDimension] Dimension028
  AngleOverride = false
  Arbitrary = false
  ArbitraryTolerances = false
  EqualTolerance = true
  ExtensionAngle = 0
  FormatSpec = %.2w
  FormatSpecOverTolerance = %+.2w
  FormatSpecUnderTolerance = %+.2w
  Inverted = false
  LineAngle = 0
  LockPosition = false
  MeasureType = 1
  OverTolerance = 0
  References2D = -> [ProjItem001]
  Rotation = 0
  ScaleType = 0
  TheoreticalExact = false
  Type = 1
  UnderTolerance = 0
  X = -93.9893
  Y = -0.649392
FEATURE [TechDraw::DrawViewDimension] Dimension029
  AngleOverride = false
  Arbitrary = false
  ArbitraryTolerances = false
  EqualTolerance = true
  ExtensionAngle = 0
  FormatSpec = %.2w
  FormatSpecOverTolerance = %+.2w
  FormatSpecUnderTolerance = %+.2w
  Inverted = false
  LineAngle = 0
  LockPosition = false
  MeasureType = 1
  OverTolerance = 0
  References2D = -> [ProjItem001]
  Rotation = 0
  ScaleType = 0
  TheoreticalExact = false
  Type = 1
  UnderTolerance = 0
  X = -37.7099
  Y = -0.447244
FEATURE [TechDraw::DrawViewDimension] Dimension030
  AngleOverride = false
  Arbitrary = false
  ArbitraryTolerances = false
  EqualTolerance = true
  ExtensionAngle = 0
  FormatSpec = %.2w
  FormatSpecOverTolerance = %+.2w
  FormatSpecUnderTolerance = %+.2w
  Inverted = false
  LineAngle = 0
  LockPosition = false
  MeasureType = 1
  OverTolerance = 0
  References2D = -> [ProjItem001]
  Rotation = 0
  ScaleType = 0
  TheoreticalExact = false
  Type = 1
  UnderTolerance = 0
  X = 22.2081
  Y = -0.447244
FEATURE [TechDraw::DrawViewDimension] Dimension031
  AngleOverride = false
  Arbitrary = false
  ArbitraryTolerances = false
  EqualTolerance = true
  ExtensionAngle = 0
  FormatSpec = %.2w
  FormatSpecOverTolerance = %+.2w
  FormatSpecUnderTolerance = %+.2w
  Inverted = false
  LineAngle = 0
  LockPosition = false
  MeasureType = 1
  OverTolerance = 0
  References2D = -> [ProjItem001]
  Rotation = 0
  ScaleType = 0
  TheoreticalExact = false
  Type = 1
  UnderTolerance = 0
  X = 82.5304
  Y = -0.447244
FEATURE [TechDraw::DrawViewDimension] Dimension032
  AngleOverride = false
  Arbitrary = false
  ArbitraryTolerances = false
  EqualTolerance = true
  ExtensionAngle = 0
  FormatSpec = %.2w
  FormatSpecOverTolerance = %+.2w
  FormatSpecUnderTolerance = %+.2w
  Inverted = false
  LineAngle = 0
  LockPosition = false
  MeasureType = 1
  OverTolerance = 0
  References2D = -> [ProjItem001]
  Rotation = 0
  ScaleType = 0
  TheoreticalExact = false
  Type = 1
  UnderTolerance = 0
  X = -93.9893
  Y = 43.6827
FEATURE [TechDraw::DrawViewDimension] Dimension033
  AngleOverride = false
  Arbitrary = false
  ArbitraryTolerances = false
  EqualTolerance = true
  ExtensionAngle = 0
  FormatSpec = %.2w
  FormatSpecOverTolerance = %+.2w
  FormatSpecUnderTolerance = %+.2w
  Inverted = false
  LineAngle = 0
  LockPosition = false
  MeasureType = 1
  OverTolerance = 0
  References2D = -> [ProjItem001]
  Rotation = 0
  ScaleType = 0
  TheoreticalExact = false
  Type = 1
  UnderTolerance = 0
  X = -35.2841
  Y = 43.8848
FEATURE [TechDraw::DrawViewDimension] Dimension034
  AngleOverride = false
  Arbitrary = false
  ArbitraryTolerances = false
  EqualTolerance = true
  ExtensionAngle = 0
  FormatSpec = %.2w
  FormatSpecOverTolerance = %+.2w
  FormatSpecUnderTolerance = %+.2w
  Inverted = false
  LineAngle = 0
  LockPosition = false
  MeasureType = 1
  OverTolerance = 0
  References2D = -> [ProjItem001]
  Rotation = 0
  ScaleType = 0
  TheoreticalExact = false
  Type = 1
  UnderTolerance = 0
  X = 22.0059
  Y = 43.6827
FEATURE [TechDraw::DrawViewDimension] Dimension035
  AngleOverride = false
  Arbitrary = false
  ArbitraryTolerances = false
  EqualTolerance = true
  ExtensionAngle = 0
  FormatSpec = %.2w
  FormatSpecOverTolerance = %+.2w
  FormatSpecUnderTolerance = %+.2w
  Inverted = false
  LineAngle = 0
  LockPosition = false
  MeasureType = 1
  OverTolerance = 0
  References2D = -> [ProjItem001]
  Rotation = 0
  ScaleType = 0
  TheoreticalExact = false
  Type = 1
  UnderTolerance = 0
  X = 83.1368
  Y = 43.6827
FEATURE [TechDraw::DrawViewDimension] Dimension036
  AngleOverride = false
  Arbitrary = false
  ArbitraryTolerances = false
  EqualTolerance = true
  ExtensionAngle = 0
  FormatSpec = %.2w
  FormatSpecOverTolerance = %+.2w
  FormatSpecUnderTolerance = %+.2w
  Inverted = false
  LineAngle = 0
  LockPosition = false
  MeasureType = 1
  OverTolerance = 0
  References2D = -> [ProjItem001]
  Rotation = 0
  ScaleType = 0
  TheoreticalExact = false
  Type = 2
  UnderTolerance = 0
  X = 105.889
  Y = 42.7827
FEATURE [TechDraw::DrawViewDimension] Dimension037
  AngleOverride = false
  Arbitrary = false
  ArbitraryTolerances = false
  EqualTolerance = true
  ExtensionAngle = 0
  FormatSpec = %.2w
  FormatSpecOverTolerance = %+.2w
  FormatSpecUnderTolerance = %+.2w
  Inverted = false
  LineAngle = 0
  LockPosition = false
  MeasureType = 1
  OverTolerance = 0
  References2D = -> [ProjItem001]
  Rotation = 0
  ScaleType = 0
  TheoreticalExact = false
  Type = 2
  UnderTolerance = 0
  X = -111.388
  Y = 22.3684
FEATURE [TechDraw::DrawViewDimension] Dimension038
  AngleOverride = false
  Arbitrary = false
  ArbitraryTolerances = false
  EqualTolerance = true
  ExtensionAngle = 0
  FormatSpec = %.2w
  FormatSpecOverTolerance = %+.2w
  FormatSpecUnderTolerance = %+.2w
  Inverted = false
  LineAngle = 0
  LockPosition = false
  MeasureType = 1
  OverTolerance = 0
  References2D = -> [ProjItem001]
  Rotation = 0
  ScaleType = 0
  TheoreticalExact = false
  Type = 2
  UnderTolerance = 0
  X = -111.297
  Y = 4.9807
FEATURE [TechDraw::DrawViewDimension] Dimension039
  AngleOverride = false
  Arbitrary = false
  ArbitraryTolerances = false
  EqualTolerance = true
  ExtensionAngle = 0
  FormatSpec = %.2w
  FormatSpecOverTolerance = %+.2w
  FormatSpecUnderTolerance = %+.2w
  Inverted = false
  LineAngle = 0
  LockPosition = false
  MeasureType = 1
  OverTolerance = 0
  References2D = -> [ProjItem001]
  Rotation = 0
  ScaleType = 0
  TheoreticalExact = false
  Type = 2
  UnderTolerance = 0
  X = 105.631
  Y = -4.16454
FEATURE [TechDraw::DrawViewDimension] Dimension040
  AngleOverride = false
  Arbitrary = false
  ArbitraryTolerances = false
  EqualTolerance = true
  ExtensionAngle = 0
  FormatSpec = %.2w
  FormatSpecOverTolerance = %+.2w
  FormatSpecUnderTolerance = %+.2w
  Inverted = false
  LineAngle = 0
  LockPosition = false
  MeasureType = 1
  OverTolerance = 0
  References2D = -> [ProjItem001]
  Rotation = 0
  ScaleType = 0
  TheoreticalExact = false
  Type = 2
  UnderTolerance = 0
  X = -111.381
  Y = -15.9671
FEATURE [TechDraw::DrawViewDimension] Dimension042
  AngleOverride = false
  Arbitrary = false
  ArbitraryTolerances = false
  EqualTolerance = true
  ExtensionAngle = 0
  FormatSpec = %.2w
  FormatSpecOverTolerance = %+.2w
  FormatSpecUnderTolerance = %+.2w
  Inverted = false
  LineAngle = 0
  LockPosition = false
  MeasureType = 1
  OverTolerance = 0
  References2D = -> [ProjItem001]
  Rotation = 0
  ScaleType = 0
  TheoreticalExact = false
  Type = 2
  UnderTolerance = 0
  X = -111.556
  Y = -37.3407
FEATURE [TechDraw::DrawViewDimension] Dimension043
  AngleOverride = false
  Arbitrary = false
  ArbitraryTolerances = false
  EqualTolerance = true
  ExtensionAngle = 0
  FormatSpec = %.2w
  FormatSpecOverTolerance = %+.2w
  FormatSpecUnderTolerance = %+.2w
  Inverted = false
  LineAngle = 0
  LockPosition = false
  MeasureType = 1
  OverTolerance = 0
  References2D = -> [ProjItem001]
  Rotation = 0
  ScaleType = 0
  TheoreticalExact = false
  Type = 2
  UnderTolerance = 0
  X = 105.638
  Y = -45.5315
FEATURE [TechDraw::DrawPage] Page001  label="Drawing_Heatsink"
  KeepUpdated = true
  NextBalloonIndex = 1
  ProjectionType = 0
  Template = -> Template001
  Views = -> [ProjGroup001,Dimension,Dimension001,Dimension002,Dimension003,Dimension004,Dimension005,Dimension006,Dimension007,Dimension008,Dimension009,Dimension010,Dimension011,Dimension012,Dimension013,Dimension014,Dimension015,Dimension016,Dimension017,Dimension018,Dimension019,Dimension020,Dimension021,Dimension022,Dimension024,Dimension025,Dimension026,Dimension028,Dimension029,Dimension030,Dimension031,+11 more]
FEATURE [TechDraw::DrawProjGroupItem] ProjItem002  label="Front002"
  CoarseView = false
  Direction = (0,0,-1)
  Focus = 100
  HardHidden = false
  IsoCount = 0
  IsoHidden = false
  IsoVisible = false
  LockPosition = true
  Perspective = false
  Rotation = 0
  RotationVector = (1,0,0)
  Scale = 1.8
  ScaleType = 2
  SeamHidden = false
  SeamVisible = true
  SmoothHidden = false
  SmoothVisible = true
  Source = -> [Cut001]
  Type = 0
  X = 0
  XDirection = (1,0,0)
  Y = 0
FEATURE [TechDraw::DrawProjGroup] ProjGroup002
  Anchor = -> ProjItem002
  AutoDistribute = true
  LockPosition = false
  ProjectionType = 0
  Rotation = 0
  Scale = 1.8
  ScaleType = 0
  Source = -> [Cut001]
  Views = -> [ProjItem002]
  X = 203.774
  Y = 174.855
  spacingX = 15
  spacingY = 15
FEATURE [TechDraw::DrawSVGTemplate] Template002
  EditableTexts = AuthorName=AUTHOR NAME,CheckDate=CHECK DATE,CreationDate=CREATION DATE,DrawingNumber=NUMBER,FC-Scale=SCALE,FC-Title=TITLE,SheetNumber=SHEET,+3 more (map truncated)
  Height = 297
  Orientation = 1
  Width = 420
FEATURE [TechDraw::DrawViewDimension] Dimension044
  AngleOverride = false
  Arbitrary = false
  ArbitraryTolerances = false
  EqualTolerance = true
  ExtensionAngle = 0
  FormatSpec = %.2w
  FormatSpecOverTolerance = %+.2w
  FormatSpecUnderTolerance = %+.2w
  Inverted = false
  LineAngle = 0
  LockPosition = false
  MeasureType = 1
  OverTolerance = 0
  References2D = -> [ProjItem002]
  Rotation = 0
  Scale = 1.8
  ScaleType = 0
  TheoreticalExact = false
  Type = 1
  UnderTolerance = 0
  X = -0.807058
  Y = 105.333
FEATURE [TechDraw::DrawViewDimension] Dimension045
  AngleOverride = false
  Arbitrary = false
  ArbitraryTolerances = false
  EqualTolerance = true
  ExtensionAngle = 0
  FormatSpec = %.2w
  FormatSpecOverTolerance = %+.2w
  FormatSpecUnderTolerance = %+.2w
  Inverted = false
  LineAngle = 0
  LockPosition = false
  MeasureType = 1
  OverTolerance = 0
  References2D = -> [ProjItem002]
  Rotation = 0
  Scale = 1.8
  ScaleType = 0
  TheoreticalExact = false
  Type = 2
  UnderTolerance = 0
  X = 196.084
  Y = 1.6626
FEATURE [TechDraw::DrawViewDimension] Dimension046
  AngleOverride = false
  Arbitrary = false
  ArbitraryTolerances = false
  EqualTolerance = true
  ExtensionAngle = 0
  FormatSpec = %.2w
  FormatSpecOverTolerance = %+.2w
  FormatSpecUnderTolerance = %+.2w
  Inverted = false
  LineAngle = 0
  LockPosition = false
  MeasureType = 1
  OverTolerance = 0
  References2D = -> [ProjItem002]
  Rotation = 0
  Scale = 1.8
  ScaleType = 0
  TheoreticalExact = false
  Type = 1
  UnderTolerance = 0
  X = -169.465
  Y = 75.5039
FEATURE [TechDraw::DrawViewDimension] Dimension047
  AngleOverride = false
  Arbitrary = false
  ArbitraryTolerances = false
  EqualTolerance = true
  ExtensionAngle = 0
  FormatSpec = %.2w
  FormatSpecOverTolerance = %+.2w
  FormatSpecUnderTolerance = %+.2w
  Inverted = false
  LineAngle = 0
  LockPosition = false
  MeasureType = 1
  OverTolerance = 0
  References2D = -> [ProjItem002]
  Rotation = 0
  Scale = 1.8
  ScaleType = 0
  TheoreticalExact = false
  Type = 1
  UnderTolerance = 0
  X = -61.9691
  Y = 75.3718
FEATURE [TechDraw::DrawViewDimension] Dimension048
  AngleOverride = false
  Arbitrary = false
  ArbitraryTolerances = false
  EqualTolerance = true
  ExtensionAngle = 0
  FormatSpec = %.2w
  FormatSpecOverTolerance = %+.2w
  FormatSpecUnderTolerance = %+.2w
  Inverted = false
  LineAngle = 0
  LockPosition = false
  MeasureType = 1
  OverTolerance = 0
  References2D = -> [ProjItem002]
  Rotation = 0
  Scale = 1.8
  ScaleType = 0
  TheoreticalExact = false
  Type = 1
  UnderTolerance = 0
  X = 46.1936
  Y = 75.4506
FEATURE [TechDraw::DrawViewDimension] Dimension049
  AngleOverride = false
  Arbitrary = false
  ArbitraryTolerances = false
  EqualTolerance = true
  ExtensionAngle = 0
  FormatSpec = %.2w
  FormatSpecOverTolerance = %+.2w
  FormatSpecUnderTolerance = %+.2w
  Inverted = false
  LineAngle = 0
  LockPosition = false
  MeasureType = 1
  OverTolerance = 0
  References2D = -> [ProjItem002]
  Rotation = 0
  Scale = 1.8
  ScaleType = 0
  TheoreticalExact = false
  Type = 1
  UnderTolerance = 0
  X = 153.252
  Y = 75.3932
FEATURE [TechDraw::DrawViewDimension] Dimension050
  AngleOverride = false
  Arbitrary = false
  ArbitraryTolerances = false
  EqualTolerance = true
  ExtensionAngle = 0
  FormatSpec = %.2w
  FormatSpecOverTolerance = %+.2w
  FormatSpecUnderTolerance = %+.2w
  Inverted = false
  LineAngle = 0
  LockPosition = false
  MeasureType = 1
  OverTolerance = 0
  References2D = -> [ProjItem002]
  Rotation = 0
  Scale = 1.8
  ScaleType = 0
  TheoreticalExact = false
  Type = 2
  UnderTolerance = 0
  X = 185.22
  Y = -83.2017
FEATURE [TechDraw::DrawViewDimension] Dimension051
  AngleOverride = false
  Arbitrary = false
  ArbitraryTolerances = false
  EqualTolerance = true
  ExtensionAngle = 0
  FormatSpec = %.2w
  FormatSpecOverTolerance = %+.2w
  FormatSpecUnderTolerance = %+.2w
  Inverted = false
  LineAngle = 0
  LockPosition = false
  MeasureType = 1
  OverTolerance = 0
  References2D = -> [ProjItem002]
  Rotation = 0
  Scale = 1.8
  ScaleType = 0
  TheoreticalExact = false
  Type = 2
  UnderTolerance = 0
  X = 185.217
  Y = -6.54888
FEATURE [TechDraw::DrawViewDimension] Dimension052
  AngleOverride = false
  Arbitrary = false
  ArbitraryTolerances = false
  EqualTolerance = true
  ExtensionAngle = 0
  FormatSpec = %.2w
  FormatSpecOverTolerance = %+.2w
  FormatSpecUnderTolerance = %+.2w
  Inverted = false
  LineAngle = 0
  LockPosition = false
  MeasureType = 1
  OverTolerance = 0
  References2D = -> [ProjItem002]
  Rotation = 0
  Scale = 1.8
  ScaleType = 0
  TheoreticalExact = false
  Type = 2
  UnderTolerance = 0
  X = 185.257
  Y = 74.8463
FEATURE [TechDraw::DrawViewDimension] Dimension053
  AngleOverride = false
  Arbitrary = false
  ArbitraryTolerances = false
  EqualTolerance = true
  ExtensionAngle = 0
  FormatSpec = %.2w
  FormatSpecOverTolerance = %+.2w
  FormatSpecUnderTolerance = %+.2w
  Inverted = false
  LineAngle = 0
  LockPosition = false
  MeasureType = 1
  OverTolerance = 0
  References2D = -> [ProjItem002]
  Rotation = 0
  Scale = 1.8
  ScaleType = 0
  TheoreticalExact = false
  Type = 1
  UnderTolerance = 0
  X = -168.79
  Y = 49.4286
FEATURE [TechDraw::DrawViewDimension] Dimension054
  AngleOverride = false
  Arbitrary = false
  ArbitraryTolerances = false
  EqualTolerance = true
  ExtensionAngle = 0
  FormatSpec = %.2w
  FormatSpecOverTolerance = %+.2w
  FormatSpecUnderTolerance = %+.2w
  Inverted = false
  LineAngle = 0
  LockPosition = false
  MeasureType = 1
  OverTolerance = 0
  References2D = -> [ProjItem002]
  Rotation = 0
  Scale = 1.8
  ScaleType = 0
  TheoreticalExact = false
  Type = 1
  UnderTolerance = 0
  X = -134.692
  Y = 16.1839
FEATURE [TechDraw::DrawViewDimension] Dimension055
  AngleOverride = false
  Arbitrary = false
  ArbitraryTolerances = false
  EqualTolerance = true
  ExtensionAngle = 0
  FormatSpec = %.2w
  FormatSpecOverTolerance = %+.2w
  FormatSpecUnderTolerance = %+.2w
  Inverted = false
  LineAngle = 0
  LockPosition = false
  MeasureType = 1
  OverTolerance = 0
  References2D = -> [ProjItem002]
  Rotation = 0
  Scale = 1.8
  ScaleType = 0
  TheoreticalExact = false
  Type = 1
  UnderTolerance = 0
  X = -99.4022
  Y = 49.4332
FEATURE [TechDraw::DrawViewDimension] Dimension056
  AngleOverride = false
  Arbitrary = false
  ArbitraryTolerances = false
  EqualTolerance = true
  ExtensionAngle = 0
  FormatSpec = %.2w
  FormatSpecOverTolerance = %+.2w
  FormatSpecUnderTolerance = %+.2w
  Inverted = false
  LineAngle = 0
  LockPosition = false
  MeasureType = 1
  OverTolerance = 0
  References2D = -> [ProjItem002]
  Rotation = 0
  Scale = 1.8
  ScaleType = 0
  TheoreticalExact = false
  Type = 1
  UnderTolerance = 0
  X = -62.9157
  Y = 16.1835
FEATURE [TechDraw::DrawViewDimension] Dimension057
  AngleOverride = false
  Arbitrary = false
  ArbitraryTolerances = false
  EqualTolerance = true
  ExtensionAngle = 0
  FormatSpec = %.2w
  FormatSpecOverTolerance = %+.2w
  FormatSpecUnderTolerance = %+.2w
  Inverted = false
  LineAngle = 0
  LockPosition = false
  MeasureType = 1
  OverTolerance = 0
  References2D = -> [ProjItem002]
  Rotation = 0
  Scale = 1.8
  ScaleType = 0
  TheoreticalExact = false
  Type = 1
  UnderTolerance = 0
  X = -25.0208
  Y = 49.3645
FEATURE [TechDraw::DrawViewDimension] Dimension058
  AngleOverride = false
  Arbitrary = false
  ArbitraryTolerances = false
  EqualTolerance = true
  ExtensionAngle = 0
  FormatSpec = %.2w
  FormatSpecOverTolerance = %+.2w
  FormatSpecUnderTolerance = %+.2w
  Inverted = false
  LineAngle = 0
  LockPosition = false
  MeasureType = 1
  OverTolerance = 0
  References2D = -> [ProjItem002]
  Rotation = 0
  Scale = 1.8
  ScaleType = 0
  TheoreticalExact = false
  Type = 1
  UnderTolerance = 0
  X = 11.5492
  Y = 16.1513
FEATURE [TechDraw::DrawViewDimension] Dimension059
  AngleOverride = false
  Arbitrary = false
  ArbitraryTolerances = false
  EqualTolerance = true
  ExtensionAngle = 0
  FormatSpec = %.2w
  FormatSpecOverTolerance = %+.2w
  FormatSpecUnderTolerance = %+.2w
  Inverted = false
  LineAngle = 0
  LockPosition = false
  MeasureType = 1
  OverTolerance = 0
  References2D = -> [ProjItem002]
  Rotation = 0
  Scale = 1.8
  ScaleType = 0
  TheoreticalExact = false
  Type = 1
  UnderTolerance = 0
  X = 44.8702
  Y = 49.413
FEATURE [TechDraw::DrawViewDimension] Dimension060
  AngleOverride = false
  Arbitrary = false
  ArbitraryTolerances = false
  EqualTolerance = true
  ExtensionAngle = 0
  FormatSpec = %.2w
  FormatSpecOverTolerance = %+.2w
  FormatSpecUnderTolerance = %+.2w
  Inverted = false
  LineAngle = 0
  LockPosition = false
  MeasureType = 1
  OverTolerance = 0
  References2D = -> [ProjItem002]
  Rotation = 0
  Scale = 1.8
  ScaleType = 0
  TheoreticalExact = false
  Type = 1
  UnderTolerance = 0
  X = 79.3191
  Y = 16.2044
FEATURE [TechDraw::DrawViewDimension] Dimension061
  AngleOverride = false
  Arbitrary = false
  ArbitraryTolerances = false
  EqualTolerance = true
  ExtensionAngle = 0
  FormatSpec = %.2w
  FormatSpecOverTolerance = %+.2w
  FormatSpecUnderTolerance = %+.2w
  Inverted = false
  LineAngle = 0
  LockPosition = false
  MeasureType = 1
  OverTolerance = 0
  References2D = -> [ProjItem002]
  Rotation = 0
  Scale = 1.8
  ScaleType = 0
  TheoreticalExact = false
  Type = 1
  UnderTolerance = 0
  X = 117.806
  Y = 49.4829
FEATURE [TechDraw::DrawViewDimension] Dimension062
  AngleOverride = false
  Arbitrary = false
  ArbitraryTolerances = false
  EqualTolerance = true
  ExtensionAngle = 0
  FormatSpec = %.2w
  FormatSpecOverTolerance = %+.2w
  FormatSpecUnderTolerance = %+.2w
  Inverted = false
  LineAngle = 0
  LockPosition = false
  MeasureType = 1
  OverTolerance = 0
  References2D = -> [ProjItem002]
  Rotation = 0
  Scale = 1.8
  ScaleType = 0
  TheoreticalExact = false
  Type = 1
  UnderTolerance = 0
  X = 153.79
  Y = 16.2459
FEATURE [TechDraw::DrawViewDimension] Dimension063
  AngleOverride = false
  Arbitrary = false
  ArbitraryTolerances = false
  EqualTolerance = true
  ExtensionAngle = 0
  FormatSpec = %.2w
  FormatSpecOverTolerance = %+.2w
  FormatSpecUnderTolerance = %+.2w
  Inverted = false
  LineAngle = 0
  LockPosition = false
  MeasureType = 1
  OverTolerance = 0
  References2D = -> [ProjItem002]
  Rotation = 0
  Scale = 1.8
  ScaleType = 0
  TheoreticalExact = false
  Type = 1
  UnderTolerance = 0
  X = -170.873
  Y = -22.7356
FEATURE [TechDraw::DrawViewDimension] Dimension064
  AngleOverride = false
  Arbitrary = false
  ArbitraryTolerances = false
  EqualTolerance = true
  ExtensionAngle = 0
  FormatSpec = %.2w
  FormatSpecOverTolerance = %+.2w
  FormatSpecUnderTolerance = %+.2w
  Inverted = false
  LineAngle = 0
  LockPosition = false
  MeasureType = 1
  OverTolerance = 0
  References2D = -> [ProjItem002]
  Rotation = 0
  Scale = 1.8
  ScaleType = 0
  TheoreticalExact = false
  Type = 1
  UnderTolerance = 0
  X = -136.25
  Y = -57.2855
FEATURE [TechDraw::DrawViewDimension] Dimension065
  AngleOverride = false
  Arbitrary = false
  ArbitraryTolerances = false
  EqualTolerance = true
  ExtensionAngle = 0
  FormatSpec = %.2w
  FormatSpecOverTolerance = %+.2w
  FormatSpecUnderTolerance = %+.2w
  Inverted = false
  LineAngle = 0
  LockPosition = false
  MeasureType = 1
  OverTolerance = 0
  References2D = -> [ProjItem002]
  Rotation = 0
  Scale = 1.8
  ScaleType = 0
  TheoreticalExact = false
  Type = 1
  UnderTolerance = 0
  X = -97.2068
  Y = -22.7688
FEATURE [TechDraw::DrawViewDimension] Dimension066
  AngleOverride = false
  Arbitrary = false
  ArbitraryTolerances = false
  EqualTolerance = true
  ExtensionAngle = 0
  FormatSpec = %.2w
  FormatSpecOverTolerance = %+.2w
  FormatSpecUnderTolerance = %+.2w
  Inverted = false
  LineAngle = 0
  LockPosition = false
  MeasureType = 1
  OverTolerance = 0
  References2D = -> [ProjItem002]
  Rotation = 0
  Scale = 1.8
  ScaleType = 0
  TheoreticalExact = false
  Type = 1
  UnderTolerance = 0
  X = -61.6785
  Y = -57.2885
FEATURE [TechDraw::DrawViewDimension] Dimension067
  AngleOverride = false
  Arbitrary = false
  ArbitraryTolerances = false
  EqualTolerance = true
  ExtensionAngle = 0
  FormatSpec = %.2w
  FormatSpecOverTolerance = %+.2w
  FormatSpecUnderTolerance = %+.2w
  Inverted = false
  LineAngle = 0
  LockPosition = false
  MeasureType = 1
  OverTolerance = 0
  References2D = -> [ProjItem002]
  Rotation = 0
  Scale = 1.8
  ScaleType = 0
  TheoreticalExact = false
  Type = 1
  UnderTolerance = 0
  X = -26.7663
  Y = -22.7449
FEATURE [TechDraw::DrawViewDimension] Dimension068
  AngleOverride = false
  Arbitrary = false
  ArbitraryTolerances = false
  EqualTolerance = true
  ExtensionAngle = 0
  FormatSpec = %.2w
  FormatSpecOverTolerance = %+.2w
  FormatSpecUnderTolerance = %+.2w
  Inverted = false
  LineAngle = 0
  LockPosition = false
  MeasureType = 1
  OverTolerance = 0
  References2D = -> [ProjItem002]
  Rotation = 0
  Scale = 1.8
  ScaleType = 0
  TheoreticalExact = false
  Type = 1
  UnderTolerance = 0
  X = 5.34468
  Y = -57.2923
FEATURE [TechDraw::DrawViewDimension] Dimension069
  AngleOverride = false
  Arbitrary = false
  ArbitraryTolerances = false
  EqualTolerance = true
  ExtensionAngle = 0
  FormatSpec = %.2w
  FormatSpecOverTolerance = %+.2w
  FormatSpecUnderTolerance = %+.2w
  Inverted = false
  LineAngle = 0
  LockPosition = false
  MeasureType = 1
  OverTolerance = 0
  References2D = -> [ProjItem002]
  Rotation = 0
  Scale = 1.8
  ScaleType = 0
  TheoreticalExact = false
  Type = 1
  UnderTolerance = 0
  X = 45.1233
  Y = -22.7576
FEATURE [TechDraw::DrawViewDimension] Dimension070
  AngleOverride = false
  Arbitrary = false
  ArbitraryTolerances = false
  EqualTolerance = true
  ExtensionAngle = 0
  FormatSpec = %.2w
  FormatSpecOverTolerance = %+.2w
  FormatSpecUnderTolerance = %+.2w
  Inverted = false
  LineAngle = 0
  LockPosition = false
  MeasureType = 1
  OverTolerance = 0
  References2D = -> [ProjItem002]
  Rotation = 0
  Scale = 1.8
  ScaleType = 0
  TheoreticalExact = false
  Type = 1
  UnderTolerance = 0
  X = 83.4448
  Y = -57.2827
FEATURE [TechDraw::DrawViewDimension] Dimension071
  AngleOverride = false
  Arbitrary = false
  ArbitraryTolerances = false
  EqualTolerance = true
  ExtensionAngle = 0
  FormatSpec = %.2w
  FormatSpecOverTolerance = %+.2w
  FormatSpecUnderTolerance = %+.2w
  Inverted = false
  LineAngle = 0
  LockPosition = false
  MeasureType = 1
  OverTolerance = 0
  References2D = -> [ProjItem002]
  Rotation = 0
  Scale = 1.8
  ScaleType = 0
  TheoreticalExact = false
  Type = 1
  UnderTolerance = 0
  X = 116.752
  Y = -22.7583
FEATURE [TechDraw::DrawViewDimension] Dimension072
  AngleOverride = false
  Arbitrary = false
  ArbitraryTolerances = false
  EqualTolerance = true
  ExtensionAngle = 0
  FormatSpec = %.2w
  FormatSpecOverTolerance = %+.2w
  FormatSpecUnderTolerance = %+.2w
  Inverted = false
  LineAngle = 0
  LockPosition = false
  MeasureType = 1
  OverTolerance = 0
  References2D = -> [ProjItem002]
  Rotation = 0
  Scale = 1.8
  ScaleType = 0
  TheoreticalExact = false
  Type = 1
  UnderTolerance = 0
  X = 152.322
  Y = -57.2784
FEATURE [TechDraw::DrawViewDimension] Dimension073
  AngleOverride = false
  Arbitrary = false
  ArbitraryTolerances = false
  EqualTolerance = true
  ExtensionAngle = 0
  FormatSpec = %.2w
  FormatSpecOverTolerance = %+.2w
  FormatSpecUnderTolerance = %+.2w
  Inverted = false
  LineAngle = 0
  LockPosition = false
  MeasureType = 1
  OverTolerance = 0
  References2D = -> [ProjItem002]
  Rotation = 0
  Scale = 1.8
  ScaleType = 0
  TheoreticalExact = false
  Type = 1
  UnderTolerance = 0
  X = -169.723
  Y = -3.14291
FEATURE [TechDraw::DrawViewDimension] Dimension074
  AngleOverride = false
  Arbitrary = false
  ArbitraryTolerances = false
  EqualTolerance = true
  ExtensionAngle = 0
  FormatSpec = %.2w
  FormatSpecOverTolerance = %+.2w
  FormatSpecUnderTolerance = %+.2w
  Inverted = false
  LineAngle = 0
  LockPosition = false
  MeasureType = 1
  OverTolerance = 0
  References2D = -> [ProjItem002]
  Rotation = 0
  Scale = 1.8
  ScaleType = 0
  TheoreticalExact = false
  Type = 1
  UnderTolerance = 0
  X = -60.9604
  Y = -3.15157
FEATURE [TechDraw::DrawViewDimension] Dimension075
  AngleOverride = false
  Arbitrary = false
  ArbitraryTolerances = false
  EqualTolerance = true
  ExtensionAngle = 0
  FormatSpec = %.2w
  FormatSpecOverTolerance = %+.2w
  FormatSpecUnderTolerance = %+.2w
  Inverted = false
  LineAngle = 0
  LockPosition = false
  MeasureType = 1
  OverTolerance = 0
  References2D = -> [ProjItem002]
  Rotation = 0
  Scale = 1.8
  ScaleType = 0
  TheoreticalExact = false
  Type = 1
  UnderTolerance = 0
  X = 44.5598
  Y = -3.13761
FEATURE [TechDraw::DrawViewDimension] Dimension076
  AngleOverride = false
  Arbitrary = false
  ArbitraryTolerances = false
  EqualTolerance = true
  ExtensionAngle = 0
  FormatSpec = %.2w
  FormatSpecOverTolerance = %+.2w
  FormatSpecUnderTolerance = %+.2w
  Inverted = false
  LineAngle = 0
  LockPosition = false
  MeasureType = 1
  OverTolerance = 0
  References2D = -> [ProjItem002]
  Rotation = 0
  Scale = 1.8
  ScaleType = 0
  TheoreticalExact = false
  Type = 1
  UnderTolerance = 0
  X = 153.096
  Y = -3.10969
FEATURE [TechDraw::DrawViewDimension] Dimension077
  AngleOverride = false
  Arbitrary = false
  ArbitraryTolerances = false
  EqualTolerance = true
  ExtensionAngle = 0
  FormatSpec = %.2w
  FormatSpecOverTolerance = %+.2w
  FormatSpecUnderTolerance = %+.2w
  Inverted = false
  LineAngle = 0
  LockPosition = false
  MeasureType = 1
  OverTolerance = 0
  References2D = -> [ProjItem002]
  Rotation = 0
  Scale = 1.8
  ScaleType = 0
  TheoreticalExact = false
  Type = 1
  UnderTolerance = 0
  X = -170.314
  Y = -90.9031
FEATURE [TechDraw::DrawViewDimension] Dimension078
  AngleOverride = false
  Arbitrary = false
  ArbitraryTolerances = false
  EqualTolerance = true
  ExtensionAngle = 0
  FormatSpec = %.2w
  FormatSpecOverTolerance = %+.2w
  FormatSpecUnderTolerance = %+.2w
  Inverted = false
  LineAngle = 0
  LockPosition = false
  MeasureType = 1
  OverTolerance = 0
  References2D = -> [ProjItem002]
  Rotation = 0
  Scale = 1.8
  ScaleType = 0
  TheoreticalExact = false
  Type = 1
  UnderTolerance = 0
  X = -62.2789
  Y = -90.9112
FEATURE [TechDraw::DrawViewDimension] Dimension079
  AngleOverride = false
  Arbitrary = false
  ArbitraryTolerances = false
  EqualTolerance = true
  ExtensionAngle = 0
  FormatSpec = %.2w
  FormatSpecOverTolerance = %+.2w
  FormatSpecUnderTolerance = %+.2w
  Inverted = false
  LineAngle = 0
  LockPosition = false
  MeasureType = 1
  OverTolerance = 0
  References2D = -> [ProjItem002]
  Rotation = 0
  Scale = 1.8
  ScaleType = 0
  TheoreticalExact = false
  Type = 1
  UnderTolerance = 0
  X = 44.2657
  Y = -90.913
FEATURE [TechDraw::DrawViewDimension] Dimension080
  AngleOverride = false
  Arbitrary = false
  ArbitraryTolerances = false
  EqualTolerance = true
  ExtensionAngle = 0
  FormatSpec = %.2w
  FormatSpecOverTolerance = %+.2w
  FormatSpecUnderTolerance = %+.2w
  Inverted = false
  LineAngle = 0
  LockPosition = false
  MeasureType = 1
  OverTolerance = 0
  References2D = -> [ProjItem002]
  Rotation = 0
  Scale = 1.8
  ScaleType = 0
  TheoreticalExact = false
  Type = 1
  UnderTolerance = 0
  X = 153.78
  Y = -90.9151
FEATURE [TechDraw::DrawViewDimension] Dimension081
  AngleOverride = false
  Arbitrary = false
  ArbitraryTolerances = false
  EqualTolerance = true
  ExtensionAngle = 0
  FormatSpec = %.2w
  FormatSpecOverTolerance = %+.2w
  FormatSpecUnderTolerance = %+.2w
  Inverted = false
  LineAngle = 0
  LockPosition = false
  MeasureType = 1
  OverTolerance = 0
  References2D = -> [ProjItem002]
  Rotation = 0
  Scale = 1.8
  ScaleType = 0
  TheoreticalExact = false
  Type = 2
  UnderTolerance = 0
  X = -187.138
  Y = -58.9724
FEATURE [TechDraw::DrawViewDimension] Dimension082
  AngleOverride = false
  Arbitrary = false
  ArbitraryTolerances = false
  EqualTolerance = true
  ExtensionAngle = 0
  FormatSpec = %.2w
  FormatSpecOverTolerance = %+.2w
  FormatSpecUnderTolerance = %+.2w
  Inverted = false
  LineAngle = 0
  LockPosition = false
  MeasureType = 1
  OverTolerance = 0
  References2D = -> [ProjItem002]
  Rotation = 0
  Scale = 1.8
  ScaleType = 0
  TheoreticalExact = false
  Type = 2
  UnderTolerance = 0
  X = -187.16
  Y = -24.7587
FEATURE [TechDraw::DrawViewDimension] Dimension083
  AngleOverride = false
  Arbitrary = false
  ArbitraryTolerances = false
  EqualTolerance = true
  ExtensionAngle = 0
  FormatSpec = %.2w
  FormatSpecOverTolerance = %+.2w
  FormatSpecUnderTolerance = %+.2w
  Inverted = false
  LineAngle = 0
  LockPosition = false
  MeasureType = 1
  OverTolerance = 0
  References2D = -> [ProjItem002]
  Rotation = 0
  Scale = 1.8
  ScaleType = 0
  TheoreticalExact = false
  Type = 2
  UnderTolerance = 0
  X = -187.182
  Y = 12.3649
FEATURE [TechDraw::DrawViewDimension] Dimension084
  AngleOverride = false
  Arbitrary = false
  ArbitraryTolerances = false
  EqualTolerance = true
  ExtensionAngle = 0
  FormatSpec = %.2w
  FormatSpecOverTolerance = %+.2w
  FormatSpecUnderTolerance = %+.2w
  Inverted = false
  LineAngle = 0
  LockPosition = false
  MeasureType = 1
  OverTolerance = 0
  References2D = -> [ProjItem002]
  Rotation = 0
  Scale = 1.8
  ScaleType = 0
  TheoreticalExact = false
  Type = 2
  UnderTolerance = 0
  X = -187.137
  Y = 45.773
FEATURE [TechDraw::DrawViewBalloon] Balloon
  BubbleShape = 7
  EndType = 0
  EndTypeScale = 1
  KinkLength = 5
  LockPosition = false
  OriginX = -89.1163
  OriginY = -44.0667
  Rotation = 0
  Scale = 1.8
  ScaleType = 0
  ShapeScale = 1
  SourceView = -> ProjItem002
  Text = 32x M3
  TextWrapLen = -1
  X = -77.758
  Y = -38.1469
FEATURE [TechDraw::DrawPage] Page002  label="Drawing_Heatsink_scaled"
  KeepUpdated = true
  NextBalloonIndex = 2
  ProjectionType = 0
  Scale = 1.8
  Template = -> Template002
  Views = -> [ProjGroup002,Dimension044,Dimension045,Dimension046,Dimension047,Dimension048,Dimension049,Dimension050,Dimension051,Dimension052,Dimension053,Dimension054,Dimension055,Dimension056,Dimension057,Dimension058,Dimension059,Dimension060,Dimension061,Dimension062,Dimension063,Dimension064,Dimension065,Dimension066,Dimension067,Dimension068,Dimension069,Dimension070,Dimension071,Dimension072,+13 more]
FEATURE [TechDraw::DrawSVGTemplate] Template003
  EditableTexts = Designed_by_Name=Designed by Name; Drawing_number=Drawing number; FC-Date=Date; FC-SC=Scale; FC-SH=Sheet; FC-Title=Title; Subtitle=Subtitle; Weight=Weight
  Height = 210
  Orientation = 1
  Width = 297
FEATURE [TechDraw::DrawProjGroupItem] ProjItem003  label="Front003"
  CoarseView = false
  Direction = (0,0,-1)
  Focus = 100
  HardHidden = false
  IsoCount = 0
  IsoHidden = false
  IsoVisible = false
  LockPosition = true
  Perspective = false
  Rotation = 0
  RotationVector = (1,0,0)
  ScaleType = 2
  SeamHidden = false
  SeamVisible = true
  SmoothHidden = false
  SmoothVisible = true
  Source = -> [Cut001]
  Type = 0
  X = 0
  XDirection = (1,0,0)
  Y = 0
FEATURE [TechDraw::DrawProjGroup] ProjGroup003
  Anchor = -> ProjItem003
  AutoDistribute = true
  LockPosition = false
  ProjectionType = 0
  Rotation = 0
  ScaleType = 0
  Source = -> [Cut001]
  Views = -> [ProjItem003]
  X = 148.89
  Y = 127.597
  spacingX = 15
  spacingY = 15
FEATURE [TechDraw::DrawViewDimension] Dimension085
  AngleOverride = false
  Arbitrary = false
  ArbitraryTolerances = false
  EqualTolerance = true
  ExtensionAngle = 0
  FormatSpec = %.2w
  FormatSpecOverTolerance = %+.2w
  FormatSpecUnderTolerance = %+.2w
  Inverted = false
  LineAngle = 0
  LockPosition = false
  MeasureType = 1
  OverTolerance = 0
  References2D = -> [ProjItem003]
  Rotation = 0
  ScaleType = 0
  TheoreticalExact = false
  Type = 1
  UnderTolerance = 0
  X = -0.779221
  Y = -54.9026
FEATURE [TechDraw::DrawViewDimension] Dimension086
  AngleOverride = false
  Arbitrary = false
  ArbitraryTolerances = false
  EqualTolerance = true
  ExtensionAngle = 0
  FormatSpec = %.2w
  FormatSpecOverTolerance = %+.2w
  FormatSpecUnderTolerance = %+.2w
  Inverted = false
  LineAngle = 0
  LockPosition = false
  MeasureType = 1
  OverTolerance = 0
  References2D = -> [ProjItem003]
  Rotation = 0
  ScaleType = 0
  TheoreticalExact = false
  Type = 2
  UnderTolerance = 0
  X = 106.234
  Y = 1.72078
FEATURE [TechDraw::DrawPage] Page003  label="Drawing_Heatsink_A4"
  KeepUpdated = true
  NextBalloonIndex = 1
  ProjectionType = 0
  Template = -> Template003
  Views = -> [ProjGroup003,Dimension085,Dimension086]
FEATURE [Sketcher::SketchObject] Sketch011
  FullyConstrained = true
  MapMode = 5
  Placement = pos=(8.2e-15,68.664,2.87787) rot=(0,0.692143,0.72176;3.14159rad)
  Support = -> [Cut]
  expr: Constraints[109] = <<Param>>.Balancer_Distance - 2 * <<Param>>.Balancer_Clearance
  expr: Constraints[110] = <<Param>>.Balancer_Distance - 2 * <<Param>>.Balancer_Clearance
  expr: Constraints[11] = <<Param>>.Panel_Mount_Diameter
  expr: Constraints[125] = 5 * <<Param>>.Balancer_Length_Increment + <<Param>>.Balancer_Length_Offset + 2 * <<Param>>.Balancer_Clearance
  expr: Constraints[126] = 6 * <<Param>>.Balancer_Length_Increment + <<Param>>.Balancer_Length_Offset + 2 * <<Param>>.Balancer_Clearance
  expr: Constraints[147] = <<Param>>.Balancer_Distance - 2 * <<Param>>.Balancer_Clearance
  expr: Constraints[148] = <<Param>>.Balancer_Distance - 2 * <<Param>>.Balancer_Clearance
  expr: Constraints[149] = 7 * <<Param>>.Balancer_Length_Increment + <<Param>>.Balancer_Length_Offset + 2 * <<Param>>.Balancer_Clearance
  expr: Constraints[150] = 8 * <<Param>>.Balancer_Length_Increment + <<Param>>.Balancer_Length_Offset + 2 * <<Param>>.Balancer_Clearance
  expr: Constraints[171] = <<Param>>.Balancer_Distance - 2 * <<Param>>.Balancer_Clearance
  expr: Constraints[172] = <<Param>>.Balancer_Distance - 2 * <<Param>>.Balancer_Clearance
  expr: Constraints[173] = 9 * <<Param>>.Balancer_Length_Increment + <<Param>>.Balancer_Length_Offset + 2 * <<Param>>.Balancer_Clearance
  expr: Constraints[174] = 10 * <<Param>>.Balancer_Length_Increment + <<Param>>.Balancer_Length_Offset + 2 * <<Param>>.Balancer_Clearance
  expr: Constraints[184] = <<Param>>.Balancer_Distance - 2 * <<Param>>.Balancer_Clearance
  expr: Constraints[185] = 11 * <<Param>>.Balancer_Length_Increment + <<Param>>.Balancer_Length_Offset + 2 * <<Param>>.Balancer_Clearance
  expr: Constraints[194] = 11 * <<Param>>.Balancer_Mil_Size + 2 * <<Param>>.Balancer_Mil_Clearance
  expr: Constraints[195] = <<Param>>.Balancer_Mil_Size + 2 * <<Param>>.Balancer_Mil_Clearance
  expr: Constraints[199] = <<Param>>.Balancer_Pin_Offset + <<Param>>.Balancer_Clearance
  expr: Constraints[226] = <<Param>>.Panel_Width
  expr: Constraints[227] = 194
  expr: Constraints[228] = <<Param>>.Panel_Length
  expr: Constraints[230] = <<Param>>.Panel_Length / 2 - <<Param>>.Panel_Mount_X
  expr: Constraints[231] = <<Param>>.Panel_Length / 2 + <<Param>>.Balancer_X
  expr: Constraints[232] = <<Param>>.Panel_Width / 2 - <<Param>>.Panel_Mount_Y
  expr: Constraints[233] = <<Param>>.Panel_Width / 2 - <<Param>>.Balancer_Y
  expr: Constraints[80] = <<Param>>.Balancer_Width + 2 * <<Param>>.Balancer_Clearance
  expr: Constraints[81] = <<Param>>.Balancer_Width + 2 * <<Param>>.Balancer_Clearance
  expr: Constraints[82] = <<Param>>.Balancer_Grid
  expr: Constraints[89] = 3 * <<Param>>.Balancer_Length_Increment + <<Param>>.Balancer_Length_Offset + 2 * <<Param>>.Balancer_Clearance
  expr: Constraints[90] = 4 * <<Param>>.Balancer_Length_Increment + <<Param>>.Balancer_Length_Offset + 2 * <<Param>>.Balancer_Clearance
  sketch-geometry (78):
    g0: Circle CenterX=-8.5 CenterY=-10.56 CenterZ=0 NormalX=0 NormalY=0 NormalZ=1 AngleXU=0 Radius=1.6
    g1: Circle CenterX=-8.5 CenterY=-25.56 CenterZ=0 NormalX=0 NormalY=0 NormalZ=1 AngleXU=0 Radius=1.6
    g2: Circle CenterX=-33 CenterY=-10.56 CenterZ=0 NormalX=0 NormalY=0 NormalZ=1 AngleXU=0 Radius=1.6
    g3: Circle CenterX=-33 CenterY=-25.56 CenterZ=0 NormalX=0 NormalY=0 NormalZ=1 AngleXU=0 Radius=1.6
    g4: Circle CenterX=-66.5 CenterY=-10.56 CenterZ=0 NormalX=0 NormalY=0 NormalZ=1 AngleXU=0 Radius=1.6
    g5: Circle CenterX=-66.5 CenterY=-25.56 CenterZ=0 NormalX=0 NormalY=0 NormalZ=1 AngleXU=0 Radius=1.6
    g6: Circle CenterX=-105 CenterY=-10.56 CenterZ=0 NormalX=0 NormalY=0 NormalZ=1 AngleXU=0 Radius=1.6
    g7: Circle CenterX=-105 CenterY=-25.56 CenterZ=0 NormalX=0 NormalY=0 NormalZ=1 AngleXU=0 Radius=1.6
    g8: Circle CenterX=-148.5 CenterY=-10.56 CenterZ=0 NormalX=0 NormalY=0 NormalZ=1 AngleXU=0 Radius=1.6
    g9: Circle CenterX=-148.5 CenterY=-25.56 CenterZ=0 NormalX=0 NormalY=0 NormalZ=1 AngleXU=0 Radius=1.6
    g10: Circle CenterX=-190.5 CenterY=-10.56 CenterZ=0 NormalX=0 NormalY=0 NormalZ=1 AngleXU=0 Radius=1.6
    g11: Circle CenterX=-190.5 CenterY=-25.56 CenterZ=0 NormalX=0 NormalY=0 NormalZ=1 AngleXU=0 Radius=1.6
    g12: LineSegment StartX=-190.5 StartY=-10.56 StartZ=0 EndX=-8.5 EndY=-10.56 EndZ=0
    g13: LineSegment StartX=-190.5 StartY=-25.56 StartZ=0 EndX=-8.5 EndY=-25.56 EndZ=0
    g14: LineSegment StartX=-190.5 StartY=-10.56 StartZ=0 EndX=-190.5 EndY=-25.56 EndZ=0
    g15: LineSegment StartX=-8.5 StartY=-10.56 StartZ=0 EndX=-8.5 EndY=-25.56 EndZ=0
    g16: LineSegment StartX=-148.5 StartY=-10.56 StartZ=0 EndX=-148.5 EndY=-25.56 EndZ=0
    g17: LineSegment StartX=-105 StartY=-10.56 StartZ=0 EndX=-105 EndY=-25.56 EndZ=0
    g18: LineSegment StartX=-66.5 StartY=-10.56 StartZ=0 EndX=-66.5 EndY=-25.56 EndZ=0
    g19: LineSegment StartX=-33 StartY=-10.56 StartZ=0 EndX=-33 EndY=-25.56 EndZ=0
    g20: LineSegment StartX=-186.65 StartY=-12.51 StartZ=0 EndX=-12.35 EndY=-12.51 EndZ=0
    g21: LineSegment StartX=-186.65 StartY=-18.66 StartZ=0 EndX=-12.35 EndY=-18.66 EndZ=0
    g22: LineSegment StartX=-186.65 StartY=-22.51 StartZ=0 EndX=-12.35 EndY=-22.51 EndZ=0
    g23: LineSegment StartX=-186.65 StartY=-28.66 StartZ=0 EndX=-12.35 EndY=-28.66 EndZ=0
    g24: LineSegment StartX=-12.35 StartY=-12.51 StartZ=0 EndX=-12.35 EndY=-28.66 EndZ=0
    g25: LineSegment StartX=-186.65 StartY=-12.51 StartZ=0 EndX=-186.65 EndY=-28.66 EndZ=0
    g26: LineSegment StartX=-25.15 StartY=-12.51 StartZ=0 EndX=-25.15 EndY=-18.66 EndZ=0
    g27: LineSegment StartX=-22.65 StartY=-22.51 StartZ=0 EndX=-22.65 EndY=-28.66 EndZ=0
    g28: LineSegment StartX=-22.65 StartY=-22.51 StartZ=0 EndX=-12.35 EndY=-22.51 EndZ=0
    g29: LineSegment StartX=-12.35 StartY=-22.51 StartZ=0 EndX=-12.35 EndY=-28.66 EndZ=0
    g30: LineSegment StartX=-12.35 StartY=-28.66 StartZ=0 EndX=-22.65 EndY=-28.66 EndZ=0
    g31: LineSegment StartX=-25.15 StartY=-12.51 StartZ=0 EndX=-12.35 EndY=-12.51 EndZ=0
    g32: LineSegment StartX=-12.35 StartY=-12.51 StartZ=0 EndX=-12.35 EndY=-18.66 EndZ=0
    g33: LineSegment StartX=-12.35 StartY=-18.66 StartZ=0 EndX=-25.15 EndY=-18.66 EndZ=0
    g34: LineSegment StartX=-40.85 StartY=-12.51 StartZ=0 EndX=-40.85 EndY=-18.66 EndZ=0
    g35: LineSegment StartX=-40.85 StartY=-22.51 StartZ=0 EndX=-40.85 EndY=-28.66 EndZ=0
    g36: LineSegment StartX=-58.65 StartY=-12.51 StartZ=0 EndX=-58.65 EndY=-18.66 EndZ=0
    g37: LineSegment StartX=-56.15 StartY=-22.51 StartZ=0 EndX=-56.15 EndY=-28.66 EndZ=0
    g38: LineSegment StartX=-56.15 StartY=-28.66 StartZ=0 EndX=-40.85 EndY=-28.66 EndZ=0
    g39: LineSegment StartX=-56.15 StartY=-22.51 StartZ=0 EndX=-40.85 EndY=-22.51 EndZ=0
    g40: LineSegment StartX=-58.65 StartY=-18.66 StartZ=0 EndX=-40.85 EndY=-18.66 EndZ=0
    g41: LineSegment StartX=-58.65 StartY=-12.51 StartZ=0 EndX=-40.85 EndY=-12.51 EndZ=0
    g42: LineSegment StartX=-74.35 StartY=-12.51 StartZ=0 EndX=-74.35 EndY=-18.66 EndZ=0
    g43: LineSegment StartX=-74.35 StartY=-22.51 StartZ=0 EndX=-74.35 EndY=-28.66 EndZ=0
    g44: LineSegment StartX=-94.65 StartY=-22.51 StartZ=0 EndX=-94.65 EndY=-28.66 EndZ=0
    g45: LineSegment StartX=-97.15 StartY=-12.51 StartZ=0 EndX=-97.15 EndY=-18.66 EndZ=0
    g46: LineSegment StartX=-94.65 StartY=-28.66 StartZ=0 EndX=-74.35 EndY=-28.66 EndZ=0
    g47: LineSegment StartX=-94.65 StartY=-22.51 StartZ=0 EndX=-74.35 EndY=-22.51 EndZ=0
    g48: LineSegment StartX=-97.15 StartY=-18.66 StartZ=0 EndX=-74.35 EndY=-18.66 EndZ=0
    g49: LineSegment StartX=-97.15 StartY=-12.51 StartZ=0 EndX=-74.35 EndY=-12.51 EndZ=0
    g50: LineSegment StartX=-112.85 StartY=-12.51 StartZ=0 EndX=-112.85 EndY=-18.66 EndZ=0
    g51: LineSegment StartX=-112.85 StartY=-22.51 StartZ=0 EndX=-112.85 EndY=-28.66 EndZ=0
    g52: LineSegment StartX=-140.65 StartY=-12.51 StartZ=0 EndX=-140.65 EndY=-18.66 EndZ=0
    g53: LineSegment StartX=-138.15 StartY=-22.51 StartZ=0 EndX=-138.15 EndY=-28.66 EndZ=0
    g54: LineSegment StartX=-138.15 StartY=-28.66 StartZ=0 EndX=-112.85 EndY=-28.66 EndZ=0
    g55: LineSegment StartX=-138.15 StartY=-22.51 StartZ=0 EndX=-112.85 EndY=-22.51 EndZ=0
    g56: LineSegment StartX=-140.65 StartY=-18.66 StartZ=0 EndX=-112.85 EndY=-18.66 EndZ=0
    g57: LineSegment StartX=-140.65 StartY=-12.51 StartZ=0 EndX=-112.85 EndY=-12.51 EndZ=0
    g58: LineSegment StartX=-186.65 StartY=-22.51 StartZ=0 EndX=-186.65 EndY=-28.66 EndZ=0
    g59: LineSegment StartX=-156.35 StartY=-22.51 StartZ=0 EndX=-156.35 EndY=-28.66 EndZ=0
    g60: LineSegment StartX=-186.65 StartY=-28.66 StartZ=0 EndX=-156.35 EndY=-28.66 EndZ=0
    g61: LineSegment StartX=-186.65 StartY=-22.51 StartZ=0 EndX=-156.35 EndY=-22.51 EndZ=0
    g62: LineSegment StartX=-185.97 StartY=-13.29 StartZ=0 EndX=-157.03 EndY=-13.29 EndZ=0
    g63: LineSegment StartX=-157.03 StartY=-13.29 StartZ=0 EndX=-157.03 EndY=-16.83 EndZ=0
    g64: LineSegment StartX=-157.03 StartY=-16.83 StartZ=0 EndX=-185.97 EndY=-16.83 EndZ=0
    g65: LineSegment StartX=-185.97 StartY=-16.83 StartZ=0 EndX=-185.97 EndY=-13.29 EndZ=0
    g66: LineSegment StartX=-186.65 StartY=-15.06 StartZ=0 EndX=-12.35 EndY=-15.06 EndZ=0
    g67: LineSegment StartX=-157.03 StartY=-13.29 StartZ=0 EndX=-171.5 EndY=-15.06 EndZ=0
    g68: LineSegment StartX=-157.03 StartY=-16.83 StartZ=0 EndX=-171.5 EndY=-15.06 EndZ=0
    g69: LineSegment StartX=-185.97 StartY=-13.29 StartZ=0 EndX=-171.5 EndY=-15.06 EndZ=0
    g70: LineSegment StartX=-156.35 StartY=-28.66 StartZ=0 EndX=-171.5 EndY=-25.585 EndZ=0
    g71: LineSegment StartX=-171.5 StartY=-25.585 StartZ=0 EndX=-156.35 EndY=-22.51 EndZ=0
    g72: LineSegment StartX=-171.5 StartY=-25.585 StartZ=0 EndX=-186.65 EndY=-22.51 EndZ=0
    g73: LineSegment StartX=-171.5 StartY=-15.06 StartZ=0 EndX=-171.5 EndY=-25.585 EndZ=0
    g74: LineSegment StartX=-194 StartY=-6.56 StartZ=0 EndX=-5 EndY=-6.56 EndZ=0
    g75: LineSegment StartX=-5 StartY=-6.56 StartZ=0 EndX=-5 EndY=-38.56 EndZ=0
    g76: LineSegment StartX=-5 StartY=-38.56 StartZ=0 EndX=-194 EndY=-38.56 EndZ=0
    g77: LineSegment StartX=-194 StartY=-38.56 StartZ=0 EndX=-194 EndY=-6.56 EndZ=0
  constraints (234):
    c: Equal(g10,g11)
    c: Equal(g10,g8)
    c: Equal(g10,g9)
    c: Equal(g10,g6)
    c: Equal(g10,g7)
    c: Equal(g10,g5)
    c: Equal(g10,g4)
    c: Equal(g10,g2)
    c: Equal(g10,g3)
    c: Equal(g10,g1)
    c: Equal(g10,g0)
    c: Diameter(g10) = 3.2
    c: Horizontal(g12)
    c: PointOnObject(g10,g12)
    c: PointOnObject(g8,g12)
    c: PointOnObject(g6,g12)
    c: PointOnObject(g4,g12)
    c: PointOnObject(g2,g12)
    c: PointOnObject(g0,g12)
    c: Horizontal(g13)
    c: Coincident(g14,g12)
    c: Coincident(g14,g13)
    c: Coincident(g15,g12)
    c: Coincident(g15,g13)
    c: Vertical(g15)
    c: Vertical(g14)
    c: PointOnObject(g11,g13)
    c: PointOnObject(g9,g13)
    c: PointOnObject(g7,g13)
    c: PointOnObject(g5,g13)
    c: PointOnObject(g3,g13)
    c: PointOnObject(g1,g13)
    c: Vertical(g16)
    c: Vertical(g17)
    c: Vertical(g18)
    c: Vertical(g19)
    c: PointOnObject(g16,g12)
    c: PointOnObject(g17,g12)
    c: PointOnObject(g18,g12)
    c: PointOnObject(g19,g12)
    c: PointOnObject(g16,g13)
    c: PointOnObject(g17,g13)
    c: PointOnObject(g18,g13)
    c: PointOnObject(g19,g13)
    c: PointOnObject(g10,g14)
    c: PointOnObject(g8,g16)
    c: PointOnObject(g9,g16)
    c: PointOnObject(g11,g14)
    c: PointOnObject(g6,g17)
    c: PointOnObject(g7,g17)
    c: PointOnObject(g4,g18)
    c: PointOnObject(g5,g18)
    c: PointOnObject(g2,g19)
    c: PointOnObject(g3,g19)
    c: PointOnObject(g0,g15)
    c: PointOnObject(g1,g15)
    c: DistanceY(g15,g15) = 15
    c: DistanceX(g2,g0) = 24.5
    c: DistanceX(g4,g2) = 33.5
    c: DistanceX(g6,g4) = 38.5
    c: DistanceX(g8,g6) = 43.5
    c: DistanceX(g10,g8) = 42
    c: Horizontal(g20)
    c: Horizontal(g21)
    c: Horizontal(g22)
    c: Horizontal(g23)
    c: Vertical(g24)
    c: Vertical(g25)
    c: PointOnObject(g20,g25)
    c: PointOnObject(g25,g20)
    c: PointOnObject(g25,g23)
    c: PointOnObject(g23,g25)
    c: PointOnObject(g22,g25)
    c: PointOnObject(g21,g25)
    c: PointOnObject(g24,g20)
    c: PointOnObject(g24,g23)
    c: PointOnObject(g23,g24)
    c: PointOnObject(g22,g24)
    c: PointOnObject(g21,g24)
    c: PointOnObject(g20,g24)
    c: DistanceY(g23,g22) = 6.15
    c: DistanceY(g21,g20) = 6.15
    c: DistanceY(g23,g21) = 10
    c: PointOnObject(g26,g20)
    c: PointOnObject(g26,g21)
    c: Vertical(g26)
    c: PointOnObject(g27,g22)
    c: PointOnObject(g27,g23)
    c: Vertical(g27)
    c: DistanceX(g27,g23) = 10.3
    c: DistanceX(g26,g21) = 12.8
    c: Coincident(g28,g27)
    c: Coincident(g29,g22)
    c: Coincident(g30,g23)
    c: Coincident(g28,g29)
    c: Coincident(g29,g30)
    c: Coincident(g30,g27)
    c: Coincident(g31,g26)
    c: Coincident(g32,g20)
    c: Coincident(g33,g21)
    c: Coincident(g31,g32)
    c: Coincident(g32,g33)
    c: Coincident(g33,g26)
    c: PointOnObject(g34,g20)
    c: PointOnObject(g34,g21)
    c: Vertical(g34)
    c: PointOnObject(g35,g22)
    c: PointOnObject(g35,g23)
    c: Vertical(g35)
    c: DistanceX(g34,g26) = 15.7
    c: DistanceX(g35,g26) = 15.7
    c: PointOnObject(g36,g20)
    c: PointOnObject(g36,g21)
    c: Vertical(g36)
    c: PointOnObject(g37,g22)
    c: PointOnObject(g37,g23)
    c: Vertical(g37)
    c: Coincident(g38,g37)
    c: Coincident(g38,g35)
    c: Coincident(g39,g37)
    c: Coincident(g39,g35)
    c: Coincident(g40,g36)
    c: Coincident(g40,g34)
    c: Coincident(g41,g36)
    c: Coincident(g41,g34)
    c: DistanceX(g37,g35) = 15.3
    c: DistanceX(g36,g34) = 17.8
    c: PointOnObject(g42,g20)
    c: PointOnObject(g42,g21)
    c: Vertical(g42)
    c: PointOnObject(g43,g22)
    c: PointOnObject(g43,g23)
    c: Vertical(g43)
    c: PointOnObject(g44,g22)
    c: PointOnObject(g44,g23)
    c: Vertical(g44)
    c: PointOnObject(g45,g20)
    c: PointOnObject(g45,g21)
    c: Vertical(g45)
    c: Coincident(g46,g44)
    c: Coincident(g46,g43)
    c: Coincident(g47,g44)
    c: Coincident(g47,g43)
    c: Coincident(g48,g45)
    c: Coincident(g48,g42)
    c: Coincident(g49,g45)
    c: Coincident(g49,g42)
    c: DistanceX(g42,g36) = 15.7
    c: DistanceX(g43,g36) = 15.7
    c: DistanceX(g46,g46) = 20.3
    c: DistanceX(g48,g48) = 22.8
    c: PointOnObject(g50,g20)
    c: PointOnObject(g50,g21)
    c: Vertical(g50)
    c: PointOnObject(g51,g22)
    c: PointOnObject(g51,g23)
    c: Vertical(g51)
    c: PointOnObject(g52,g20)
    c: PointOnObject(g52,g21)
    c: Vertical(g52)
    c: PointOnObject(g53,g22)
    c: PointOnObject(g53,g23)
    c: Vertical(g53)
    c: Coincident(g54,g53)
    c: Coincident(g54,g51)
    c: Coincident(g55,g53)
    c: Coincident(g55,g51)
    c: Coincident(g56,g52)
    c: Coincident(g56,g50)
    c: Coincident(g57,g52)
    c: Coincident(g57,g50)
    c: DistanceX(g50,g45) = 15.7
    c: DistanceX(g51,g45) = 15.7
    c: DistanceX(g54,g54) = 25.3
    c: DistanceX(g56,g56) = 27.8
    c: Coincident(g58,g22)
    c: Coincident(g58,g23)
    c: PointOnObject(g59,g22)
    c: PointOnObject(g59,g23)
    c: Vertical(g59)
    c: Coincident(g60,g58)
    c: Coincident(g60,g59)
    c: Coincident(g61,g58)
    c: Coincident(g61,g59)
    c: DistanceX(g59,g52) = 15.7
    c: DistanceX(g60,g60) = 30.3
    c: Horizontal(g62)
    c: Coincident(g63,g62)
    c: Vertical(g63)
    c: Coincident(g64,g63)
    c: Horizontal(g64)
    c: Coincident(g65,g64)
    c: Coincident(g65,g62)
    c: Vertical(g65)
    c: DistanceX(g64,g64) = 28.94
    c: DistanceY(g63,g63) = 3.54
    c: PointOnObject(g66,g25)
    c: PointOnObject(g66,g24)
    c: Horizontal(g66)
    c: DistanceY(g32,g66) = 3.6
    c: Coincident(g67,g62)
    c: PointOnObject(g67,g66)
    c: Coincident(g68,g63)
    c: Coincident(g68,g67)
    c: Equal(g67,g68)
    c: Coincident(g69,g62)
    c: Coincident(g69,g67)
    c: Equal(g67,g69)
    c: Coincident(g70,g59)
    c: Coincident(g71,g70)
    c: Coincident(g71,g59)
    c: Coincident(g72,g70)
    c: Coincident(g72,g58)
    c: Equal(g72,g70)
    c: Equal(g70,g71)
    c: Coincident(g73,g67)
    c: Coincident(g73,g70)
    c: Vertical(g73)
    c: Horizontal(g74)
    c: Coincident(g75,g74)
    c: Vertical(g75)
    c: Coincident(g76,g75)
    c: Horizontal(g76)
    c: Coincident(g77,g76)
    c: Coincident(g77,g74)
    c: Vertical(g77)
    c: DistanceY(g75,g75) = 32
    c: DistanceX(g74,g-1) = 194
    c: DistanceX(g76,g76) = 189
    c: DistanceY(g75,g-1) = 38.56
    c: DistanceX(g0,g74) = 3.5
    c: DistanceX(g67,g74) = 166.5
    c: DistanceY(g0,g74) = 4
    c: DistanceY(g67,g74) = 8.5
FEATURE [Part::Extrusion] Extrude012
  Base = -> Sketch011
  Dir = (1e-16,0.999123,0.0418757)
  DirMode = 2
  FaceMakerClass = Part::FaceMakerBullseye
  LengthFwd = 10
  LengthRev = 0
  Solid = true
  Symmetric = true
FEATURE [Part::Cut] Cut002  label="Housing_Cutout_Balancer"
  Base = -> Cut
  Tool = -> Extrude012
FEATURE [Part::Feature] Part__Feature032  label="Open CASCADE STEP translator 7.5 1.1.1"
  Placement = pos=(0,0,-1.64144) rot=(0,0,1;0rad)
  shape: bbox 189 x 32 x 1.641 mm, 103 faces (baked)
FEATURE [App::Part] BoardLiPoKiller_Panel
  Group = -> [Part__Feature032]
  Origin = -> Origin006
FEATURE [Part::Feature] Part__Feature033  label="6724181264"
  Placement = pos=(91,-3,0) rot=(0,0,1;0rad)
  shape: bbox 6.351 x 5.5 x 5 mm, 44 faces (baked)
FEATURE [App::Part] M12LiPoKiller_Panel
  Group = -> [Part__Feature033]
  Origin = -> Origin007
FEATURE [Part::Feature] Part__Feature034  label="6724181264001"
  Placement = pos=(66.5,-3,0) rot=(0,0,1;0rad)
  shape: bbox 6.351 x 5.5 x 5 mm, 44 faces (baked)
FEATURE [App::Part] M11LiPoKiller_Panel
  Group = -> [Part__Feature034]
  Origin = -> Origin008
FEATURE [Part::Feature] Part__Feature035  label="6724181264002"
  Placement = pos=(33,-3,0) rot=(0,0,1;0rad)
  shape: bbox 6.351 x 5.5 x 5 mm, 44 faces (baked)
FEATURE [App::Part] M10LiPoKiller_Panel
  Group = -> [Part__Feature035]
  Origin = -> Origin009
FEATURE [Part::Feature] Part__Feature036  label="6724181264003"
  Placement = pos=(-5.5,-3,0) rot=(0,0,1;0rad)
  shape: bbox 6.351 x 5.5 x 5 mm, 44 faces (baked)
FEATURE [App::Part] M9LiPoKiller_Panel
  Group = -> [Part__Feature036]
  Origin = -> Origin010
FEATURE [Part::Feature] Part__Feature037  label="6724181264004"
  Placement = pos=(-49,-3,0) rot=(0,0,1;0rad)
  shape: bbox 6.351 x 5.5 x 5 mm, 44 faces (baked)
FEATURE [App::Part] M8LiPoKiller_Panel
  Group = -> [Part__Feature037]
  Origin = -> Origin011
FEATURE [Part::Feature] Part__Feature038  label="6724181264005"
  Placement = pos=(-91,-3,0) rot=(0,0,1;0rad)
  shape: bbox 6.351 x 5.5 x 5 mm, 44 faces (baked)
FEATURE [App::Part] M7LiPoKiller_Panel
  Group = -> [Part__Feature038]
  Origin = -> Origin012
FEATURE [Part::Feature] Part__Feature039  label="6724181264006"
  Placement = pos=(91,12,0) rot=(0,0,1;0rad)
  shape: bbox 6.351 x 5.5 x 5 mm, 44 faces (baked)
FEATURE [App::Part] M6LiPoKiller_Panel
  Group = -> [Part__Feature039]
  Origin = -> Origin013
FEATURE [Part::Feature] Part__Feature040  label="6724181264007"
  Placement = pos=(66.5,12,0) rot=(0,0,1;0rad)
  shape: bbox 6.351 x 5.5 x 5 mm, 44 faces (baked)
FEATURE [App::Part] M5LiPoKiller_Panel
  Group = -> [Part__Feature040]
  Origin = -> Origin014
FEATURE [Part::Feature] Part__Feature041  label="6724181264008"
  Placement = pos=(33,12,0) rot=(0,0,1;0rad)
  shape: bbox 6.351 x 5.5 x 5 mm, 44 faces (baked)
FEATURE [App::Part] M4LiPoKiller_Panel
  Group = -> [Part__Feature041]
  Origin = -> Origin015
FEATURE [Part::Feature] Part__Feature042  label="6724181264009"
  Placement = pos=(-5.5,12,0) rot=(0,0,1;0rad)
  shape: bbox 6.351 x 5.5 x 5 mm, 44 faces (baked)
FEATURE [App::Part] M3LiPoKiller_Panel
  Group = -> [Part__Feature042]
  Origin = -> Origin016
FEATURE [Part::Feature] Part__Feature043  label="6724181264010"
  Placement = pos=(-49,12,0) rot=(0,0,1;0rad)
  shape: bbox 6.351 x 5.5 x 5 mm, 44 faces (baked)
FEATURE [App::Part] M2LiPoKiller_Panel
  Group = -> [Part__Feature043]
  Origin = -> Origin017
FEATURE [Part::Feature] Part__Feature044  label="6724181264011"
  Placement = pos=(-91,12,0) rot=(0,0,1;0rad)
  shape: bbox 6.351 x 5.5 x 5 mm, 44 faces (baked)
FEATURE [App::Part] M1LiPoKiller_Panel
  Group = -> [Part__Feature044]
  Origin = -> Origin018
FEATURE [Part::Feature] Part__Feature045  label="Extruded"
  shape: bbox 0.7 x 0.7 x 13 mm, 6 faces (baked)
FEATURE [App::Part] _590249040  label="5590249040"
  Group = -> [Part__Feature045]
  Origin = -> Origin019
  Placement = pos=(-61.84,7.5,-3) rot=(0,0,1;0rad)
FEATURE [Part::Feature] Part__Feature046  label="Extruded001"
  shape: bbox 2.54 x 2.54 x 2.5 mm, 10 faces (baked)
FEATURE [App::Part] _590248880  label="5590248880"
  Group = -> [Part__Feature046]
  Origin = -> Origin020
  Placement = pos=(-61.84,7.5,0) rot=(0,0,1;0rad)
FEATURE [Part::Feature] Part__Feature047  label="Extruded002"
  shape: bbox 0.7 x 0.7 x 13 mm, 6 faces (baked)
FEATURE [App::Part] _590249040001  label="5590249040001"
  Group = -> [Part__Feature047]
  Origin = -> Origin021
  Placement = pos=(-64.38,7.5,-3) rot=(0,0,1;0rad)
FEATURE [Part::Feature] Part__Feature048  label="Extruded003"
  shape: bbox 2.54 x 2.54 x 2.5 mm, 10 faces (baked)
FEATURE [App::Part] _590248880001  label="5590248880001"
  Group = -> [Part__Feature048]
  Origin = -> Origin022
  Placement = pos=(-64.38,7.5,0) rot=(0,0,1;0rad)
FEATURE [Part::Feature] Part__Feature049  label="Extruded004"
  shape: bbox 0.7 x 0.7 x 13 mm, 6 faces (baked)
FEATURE [App::Part] _590249040002  label="5590249040002"
  Group = -> [Part__Feature049]
  Origin = -> Origin023
  Placement = pos=(-66.92,7.5,-3) rot=(0,0,1;0rad)
FEATURE [Part::Feature] Part__Feature050  label="Extruded005"
  shape: bbox 2.54 x 2.54 x 2.5 mm, 10 faces (baked)
FEATURE [App::Part] _590248880002  label="5590248880002"
  Group = -> [Part__Feature050]
  Origin = -> Origin024
  Placement = pos=(-66.92,7.5,0) rot=(0,0,1;0rad)
FEATURE [Part::Feature] Part__Feature051  label="Extruded006"
  shape: bbox 0.7 x 0.7 x 13 mm, 6 faces (baked)
FEATURE [App::Part] _590249040003  label="5590249040003"
  Group = -> [Part__Feature051]
  Origin = -> Origin025
  Placement = pos=(-69.46,7.5,-3) rot=(0,0,1;0rad)
FEATURE [Part::Feature] Part__Feature052  label="Extruded007"
  shape: bbox 2.54 x 2.54 x 2.5 mm, 10 faces (baked)
FEATURE [App::Part] _590248880003  label="5590248880003"
  Group = -> [Part__Feature052]
  Origin = -> Origin026
  Placement = pos=(-69.46,7.5,0) rot=(0,0,1;0rad)
FEATURE [Part::Feature] Part__Feature053  label="Extruded008"
  shape: bbox 0.7 x 0.7 x 13 mm, 6 faces (baked)
FEATURE [App::Part] _590249040004  label="5590249040004"
  Group = -> [Part__Feature053]
  Origin = -> Origin027
  Placement = pos=(-72,7.5,-3) rot=(0,0,1;0rad)
FEATURE [Part::Feature] Part__Feature054  label="Extruded009"
  shape: bbox 2.54 x 2.54 x 2.5 mm, 10 faces (baked)
FEATURE [App::Part] _590248880004  label="5590248880004"
  Group = -> [Part__Feature054]
  Origin = -> Origin028
  Placement = pos=(-72,7.5,0) rot=(0,0,1;0rad)
FEATURE [Part::Feature] Part__Feature055  label="Extruded010"
  shape: bbox 0.7 x 0.7 x 13 mm, 6 faces (baked)
FEATURE [App::Part] _590249040005  label="5590249040005"
  Group = -> [Part__Feature055]
  Origin = -> Origin029
  Placement = pos=(-74.54,7.5,-3) rot=(0,0,1;0rad)
FEATURE [Part::Feature] Part__Feature056  label="Extruded011"
  shape: bbox 2.54 x 2.54 x 2.5 mm, 10 faces (baked)
FEATURE [App::Part] _590248880005  label="5590248880005"
  Group = -> [Part__Feature056]
  Origin = -> Origin030
  Placement = pos=(-74.54,7.5,0) rot=(0,0,1;0rad)
FEATURE [Part::Feature] Part__Feature057  label="Extruded012"
  shape: bbox 0.7 x 0.7 x 13 mm, 6 faces (baked)
FEATURE [App::Part] _590249040006  label="5590249040006"
  Group = -> [Part__Feature057]
  Origin = -> Origin031
  Placement = pos=(-77.08,7.5,-3) rot=(0,0,1;0rad)
FEATURE [Part::Feature] Part__Feature058  label="Extruded013"
  shape: bbox 2.54 x 2.54 x 2.5 mm, 10 faces (baked)
FEATURE [App::Part] _590248880006  label="5590248880006"
  Group = -> [Part__Feature058]
  Origin = -> Origin032
  Placement = pos=(-77.08,7.5,0) rot=(0,0,1;0rad)
FEATURE [Part::Feature] Part__Feature059  label="Extruded014"
  shape: bbox 0.7 x 0.7 x 13 mm, 6 faces (baked)
FEATURE [App::Part] _590249040007  label="5590249040007"
  Group = -> [Part__Feature059]
  Origin = -> Origin033
  Placement = pos=(-79.62,7.5,-3) rot=(0,0,1;0rad)
FEATURE [Part::Feature] Part__Feature060  label="Extruded015"
  shape: bbox 2.54 x 2.54 x 2.5 mm, 10 faces (baked)
FEATURE [App::Part] _590248880007  label="5590248880007"
  Group = -> [Part__Feature060]
  Origin = -> Origin034
  Placement = pos=(-79.62,7.5,0) rot=(0,0,1;0rad)
FEATURE [Part::Feature] Part__Feature061  label="Extruded016"
  shape: bbox 0.7 x 0.7 x 13 mm, 6 faces (baked)
FEATURE [App::Part] _590249040008  label="5590249040008"
  Group = -> [Part__Feature061]
  Origin = -> Origin035
  Placement = pos=(-82.16,7.5,-3) rot=(0,0,1;0rad)
FEATURE [Part::Feature] Part__Feature062  label="Extruded017"
  shape: bbox 2.54 x 2.54 x 2.5 mm, 10 faces (baked)
FEATURE [App::Part] _590248880008  label="5590248880008"
  Group = -> [Part__Feature062]
  Origin = -> Origin036
  Placement = pos=(-82.16,7.5,0) rot=(0,0,1;0rad)
FEATURE [Part::Feature] Part__Feature063  label="Extruded018"
  shape: bbox 0.7 x 0.7 x 13 mm, 6 faces (baked)
FEATURE [App::Part] _590249040009  label="5590249040009"
  Group = -> [Part__Feature063]
  Origin = -> Origin037
  Placement = pos=(-84.7,7.5,-3) rot=(0,0,1;0rad)
FEATURE [Part::Feature] Part__Feature064  label="Extruded019"
  shape: bbox 2.54 x 2.54 x 2.5 mm, 10 faces (baked)
FEATURE [App::Part] _590248880009  label="5590248880009"
  Group = -> [Part__Feature064]
  Origin = -> Origin038
  Placement = pos=(-84.7,7.5,0) rot=(0,0,1;0rad)
FEATURE [Part::Feature] Part__Feature065  label="Extruded020"
  shape: bbox 0.7 x 0.7 x 13 mm, 6 faces (baked)
FEATURE [App::Part] _590249040010  label="5590249040010"
  Group = -> [Part__Feature065]
  Origin = -> Origin039
  Placement = pos=(-59.3,7.5,-3) rot=(0,0,1;0rad)
FEATURE [Part::Feature] Part__Feature066  label="Extruded021"
  shape: bbox 2.54 x 2.54 x 2.5 mm, 10 faces (baked)
FEATURE [App::Part] _590248880010  label="5590248880010"
  Group = -> [Part__Feature066]
  Origin = -> Origin040
  Placement = pos=(-59.3,7.5,0) rot=(0,0,1;0rad)
FEATURE [App::Part] P10LiPoKiller_Panel
  Group = -> [_590249040,_590248880,_590249040001,_590248880001,_590249040002,_590248880002,_590249040003,_590248880003,_590249040004,_590248880004,_590249040005,_590248880005,_590249040006,_590248880006,_590249040007,_590248880007,_590249040008,_590248880008,_590249040009,_590248880009,_590249040010,_590248880010]
  Origin = -> Origin041
FEATURE [Part::Feature] Part__Feature067  label="B11B-XH-A"
  Placement = pos=(-72,-3.025,0) rot=(0,0.707107,0.707107;3.14159rad)
  shape: bbox 29.9 x 5.75 x 10.4 mm, 134 faces (baked)
FEATURE [App::Part] P9LiPoKiller_Panel
  Group = -> [Part__Feature067]
  Origin = -> Origin042
FEATURE [Part::Feature] Part__Feature068  label="B10B-XH-A"
  Placement = pos=(-27.25,6.975,0.0127) rot=(0,0.707107,0.707107;3.14159rad)
  shape: bbox 27.4 x 5.75 x 10.4 mm, 124 faces (baked)
FEATURE [App::Part] P8LiPoKiller_Panel
  Group = -> [Part__Feature068]
  Origin = -> Origin043
FEATURE [Part::Feature] Part__Feature069  label="B9B-XH-A"
  Placement = pos=(-26,-2.525,1.1127) rot=(0,0.707107,0.707107;3.14159rad)
  shape: bbox 24.9 x 5.75 x 10.4 mm, 114 faces (baked)
FEATURE [App::Part] P7LiPoKiller_Panel
  Group = -> [Part__Feature069]
  Origin = -> Origin044
FEATURE [Part::Feature] Part__Feature070  label="B8B-XH-A"
  Placement = pos=(13.75,6.975,0) rot=(0,0.707107,0.707107;3.14159rad)
  shape: bbox 22.4 x 5.75 x 10.4 mm, 104 faces (baked)
FEATURE [App::Part] P6LiPoKiller_Panel
  Group = -> [Part__Feature070]
  Origin = -> Origin045
FEATURE [Part::Feature] Part__Feature071  label="B7B-XH-A"
  Placement = pos=(15,-3.025,0) rot=(0,0.707107,0.707107;3.14159rad)
  shape: bbox 19.9 x 5.75 x 10.4 mm, 94 faces (baked)
FEATURE [App::Part] P5LiPoKiller_Panel
  Group = -> [Part__Feature071]
  Origin = -> Origin046
FEATURE [Part::Feature] Part__Feature072  label="B6B-XH-A"
  Placement = pos=(49.75,6.975,0) rot=(0,0.707107,0.707107;3.14159rad)
  shape: bbox 17.4 x 5.75 x 10.4 mm, 84 faces (baked)
FEATURE [App::Part] P4LiPoKiller_Panel
  Group = -> [Part__Feature072]
  Origin = -> Origin047
FEATURE [Part::Feature] Part__Feature073  label="B5B-XH-A"
  Placement = pos=(51,-3.025,0) rot=(0,0.707107,0.707107;3.14159rad)
  shape: bbox 14.9 x 5.75 x 10.4 mm, 74 faces (baked)
FEATURE [App::Part] P3LiPoKiller_Panel
  Group = -> [Part__Feature073]
  Origin = -> Origin048
FEATURE [Part::Feature] Part__Feature074  label="B4B-XH-A"
  Placement = pos=(80.75,6.975,0) rot=(0,0.707107,0.707107;3.14159rad)
  shape: bbox 12.4 x 5.75 x 10.4 mm, 64 faces (baked)
FEATURE [App::Part] P2LiPoKiller_Panel
  Group = -> [Part__Feature074]
  Origin = -> Origin049
FEATURE [Part::Feature] Part__Feature075  label="B3B-XH-A"
  Placement = pos=(82,-3.025,0) rot=(0,0.707107,0.707107;3.14159rad)
  shape: bbox 9.9 x 5.75 x 10.4 mm, 54 faces (baked)
FEATURE [App::Part] P1LiPoKiller_Panel
  Group = -> [Part__Feature075]
  Origin = -> Origin050
FEATURE [App::Part] PCB
  Group = -> [BoardLiPoKiller_Panel,M12LiPoKiller_Panel,M11LiPoKiller_Panel,M10LiPoKiller_Panel,M9LiPoKiller_Panel,M8LiPoKiller_Panel,M7LiPoKiller_Panel,M6LiPoKiller_Panel,M5LiPoKiller_Panel,M4LiPoKiller_Panel,M3LiPoKiller_Panel,M2LiPoKiller_Panel,M1LiPoKiller_Panel,P10LiPoKiller_Panel,P9LiPoKiller_Panel,P8LiPoKiller_Panel,P7LiPoKiller_Panel,P6LiPoKiller_Panel,P5LiPoKiller_Panel,P4LiPoKiller_Panel,+3 more]
  Origin = -> Origin051
  Placement = pos=(99.5,61.61,-20) rot=(0,-0.691905,-0.721988;3.14159rad)
